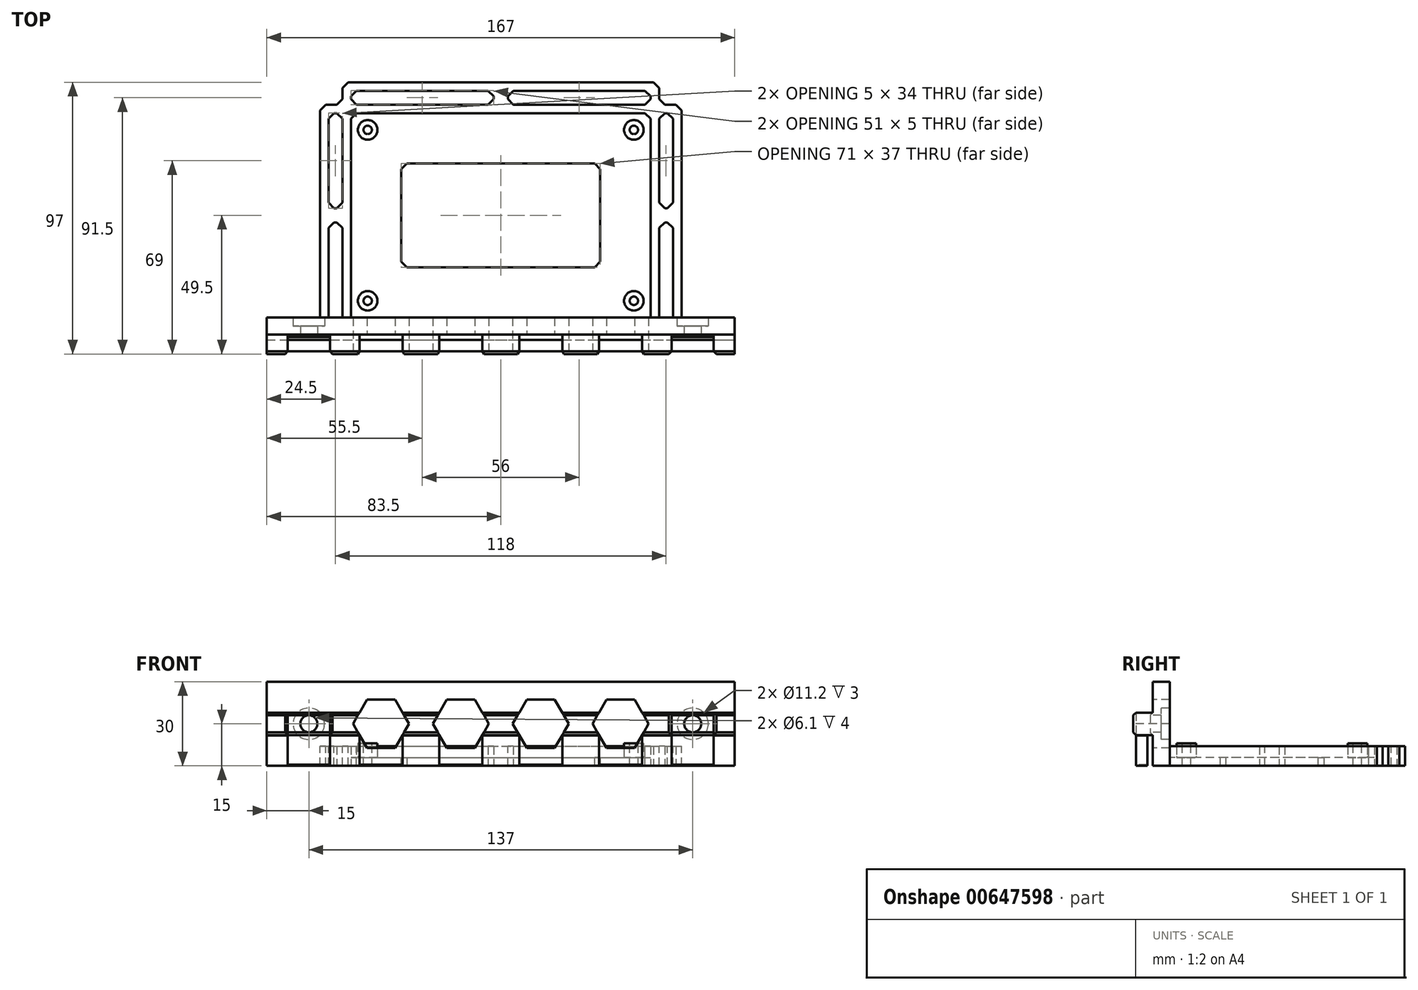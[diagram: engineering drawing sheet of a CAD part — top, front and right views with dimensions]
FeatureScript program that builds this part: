
annotation { "Feature Type Name" : "Feature", "Feature Type Description" : "" }
export const myFeature = defineFeature(function(context is Context, id is Id, definition is map)
    precondition{}
    {
        {
            var Q0;
            Q0=qCreatedBy(makeId("Top.planeOp"),FACE);
            var sketch = newSketch(context, id + "F0", { "sketchPlane" : qUnion([Q0])});
            skLineSegment(sketch, "E0.bottom", {"start": v(-47.5, 30.5) * mm, "end": v(47.5, 30.5) * mm, "construction": true});
            skLineSegment(sketch, "E0.top", {"start": v(-47.5, -30.5) * mm, "end": v(47.5, -30.5) * mm, "construction": true});
            skLineSegment(sketch, "E0.left", {"start": v(-47.5, 30.5) * mm, "end": v(-47.5, -30.5) * mm, "construction": true});
            skLineSegment(sketch, "E0.right", {"start": v(47.5, 30.5) * mm, "end": v(47.5, -30.5) * mm, "construction": true});
            skPoint(sketch, "E0.middle", {"position": v(0, 0) * mm});
            skCircle(sketch, "E1", {"center": v(-47.5, 30.5) * mm, "radius": 1.5 * mm});
            skCircle(sketch, "E2", {"center": v(47.5, 30.5) * mm, "radius": 1.5 * mm});
            skCircle(sketch, "E3", {"center": v(47.5, -30.5) * mm, "radius": 1.5 * mm});
            skCircle(sketch, "E4", {"center": v(-47.5, -30.5) * mm, "radius": 1.5 * mm});
            skCircle(sketch, "E5", {"center": v(-47.5, 30.5) * mm, "radius": 3.5 * mm});
            skCircle(sketch, "E6", {"center": v(47.5, 30.5) * mm, "radius": 3.5 * mm});
            skCircle(sketch, "E7", {"center": v(47.5, -30.5) * mm, "radius": 3.5 * mm});
            skCircle(sketch, "E8", {"center": v(-47.5, -30.5) * mm, "radius": 3.5 * mm});
            skLineSegment(sketch, "E9.0", {"start": v(-53.5, 44.5) * mm, "end": v(-53.5, -36.5) * mm});
            skLineSegment(sketch, "E9.1", {"start": v(-61.5, 36.5) * mm, "end": v(61.5, 36.5) * mm});
            skLineSegment(sketch, "E9.2", {"start": v(53.5, 44.5) * mm, "end": v(53.5, -36.5) * mm});
            skLineSegment(sketch, "E9.3", {"start": v(-83.5, -36.5) * mm, "end": v(83.5, -36.5) * mm});
            skLineSegment(sketch, "E10.0", {"start": v(-56.5, 47.5) * mm, "end": v(-56.5, -36.5) * mm});
            skLineSegment(sketch, "E10.1", {"start": v(-64.5, 39.5) * mm, "end": v(64.5, 39.5) * mm});
            skLineSegment(sketch, "E10.2", {"start": v(56.5, 47.5) * mm, "end": v(56.5, -36.5) * mm});
            skLineSegment(sketch, "E11.0", {"start": v(-61.5, 36.5) * mm, "end": v(-61.5, -36.5) * mm});
            skLineSegment(sketch, "E11.1", {"start": v(-53.5, 44.5) * mm, "end": v(53.5, 44.5) * mm});
            skLineSegment(sketch, "E11.2", {"start": v(61.5, 36.5) * mm, "end": v(61.5, -36.5) * mm});
            skLineSegment(sketch, "E12.0", {"start": v(-64.5, 39.5) * mm, "end": v(-64.5, -36.5) * mm});
            skLineSegment(sketch, "E12.1", {"start": v(-56.5, 47.5) * mm, "end": v(56.5, 47.5) * mm});
            skLineSegment(sketch, "E12.2", {"start": v(64.5, 39.5) * mm, "end": v(64.5, -36.5) * mm});
            skLineSegment(sketch, "E13.0", {"start": v(-35.5, 18.5) * mm, "end": v(-35.5, -18.5) * mm});
            skLineSegment(sketch, "E13.1", {"start": v(-35.5, 18.5) * mm, "end": v(35.5, 18.5) * mm});
            skLineSegment(sketch, "E13.2", {"start": v(35.5, 18.5) * mm, "end": v(35.5, -18.5) * mm});
            skLineSegment(sketch, "E13.3", {"start": v(-35.5, -18.5) * mm, "end": v(35.5, -18.5) * mm});
            skLineSegment(sketch, "E14", {"start": v(-83.5, -36.5) * mm, "end": v(-83.5, -42.5) * mm});
            skLineSegment(sketch, "E15", {"start": v(-83.5, -42.5) * mm, "end": v(83.5, -42.5) * mm});
            skLineSegment(sketch, "E16", {"start": v(83.5, -42.5) * mm, "end": v(83.5, -36.5) * mm});
            skPoint(sketch, "E17", {"position": v(0, -42.5) * mm});
            skLineSegment(sketch, "E18", {"start": v(-61.5, 2.5) * mm, "end": v(-56.5, 2.5) * mm});
            skLineSegment(sketch, "E19", {"start": v(-56.5, -2.5) * mm, "end": v(-61.5, -2.5) * mm});
            skLineSegment(sketch, "E20", {"start": v(-2.5, 44.5) * mm, "end": v(-2.5, 39.5) * mm});
            skLineSegment(sketch, "E21", {"start": v(2.5, 39.5) * mm, "end": v(2.5, 44.5) * mm});
            skLineSegment(sketch, "E22", {"start": v(56.5, 2.5) * mm, "end": v(61.5, 2.5) * mm});
            skLineSegment(sketch, "E23", {"start": v(61.5, -2.5) * mm, "end": v(56.5, -2.5) * mm});
            skPoint(sketch, "E24", {"position": v(0, 44.5) * mm});
            skPoint(sketch, "E25", {"position": v(-61.5, 0) * mm});
            skLineSegment(sketch, "E26", {"start": v(-61.5, 2.5) * mm, "end": v(-61.5, -2.5) * mm, "construction": true});
            skLineSegment(sketch, "E27", {"start": v(-2.5, 44.5) * mm, "end": v(2.5, 44.5) * mm, "construction": true});
            skSolve(sketch);
        }
        {
            var Q0;
            Q0=makeQuery(id+"F0.imprint","IMPRINT",FACE,{"disambiguationData":[TD([[makeQuery(id+"F0.imprint","IMPRINT",EDGE,{"derivedFrom":sQuery(id+"F0.wireOp",EDGE,"E5")}),-1.0]])]});
            var Q1;
            Q1=makeQuery(id+"F0.imprint","IMPRINT",FACE,{"disambiguationData":[TD([[makeQuery(id+"F0.imprint","IMPRINT",EDGE,{"derivedFrom":sQuery(id+"F0.wireOp",EDGE,"E1")}),-1.0]])]});
            var Q2;
            Q2=makeQuery(id+"F0.imprint","IMPRINT",FACE,{"disambiguationData":[TD([[makeQuery(id+"F0.imprint","IMPRINT",EDGE,{"derivedFrom":sQuery(id+"F0.wireOp",EDGE,"E4")}),-1.0]])]});
            var Q3;
            Q3=makeQuery(id+"F0.imprint","IMPRINT",FACE,{"disambiguationData":[TD([[makeQuery(id+"F0.imprint","IMPRINT",EDGE,{"derivedFrom":sQuery(id+"F0.wireOp",EDGE,"E3")}),-1.0]])]});
            var Q4;
            Q4=makeQuery(id+"F0.imprint","IMPRINT",FACE,{"disambiguationData":[TD([[makeQuery(id+"F0.imprint","IMPRINT",EDGE,{"derivedFrom":sQuery(id+"F0.wireOp",EDGE,"E2")}),-1.0]])]});
            var Q5;
            {var subQ0=sQuery(id+"F0.wireOp",EDGE,"E9.3");var subQ1=sQuery(id+"F0.wireOp",EDGE,"E9.0");var subQ2=makeQuery(id+"F0.imprint","INTERSECT",VERTEX,{"derivedFrom":[subQ1,subQ0]});Q5=makeQuery(id+"F0.imprint","IMPRINT",FACE,{"disambiguationData":[TD([[makeQuery(id+"F0.imprint","IMPRINT",EDGE,{"disambiguationData":[TD([[subQ2,1.0]])],"derivedFrom":subQ1}),-1.0]])]});}
            var Q6;
            {var subQ0=sQuery(id+"F0.wireOp",EDGE,"E12.0");Q6=makeQuery(id+"F0.imprint","IMPRINT",FACE,{"disambiguationData":[TD([[makeQuery(id+"F0.imprint","IMPRINT",EDGE,{"derivedFrom":subQ0}),1.0]])]});}
            var Q7;
            {var subQ0=sQuery(id+"F0.wireOp",EDGE,"E18");Q7=makeQuery(id+"F0.imprint","IMPRINT",FACE,{"disambiguationData":[TD([[makeQuery(id+"F0.imprint","IMPRINT",EDGE,{"derivedFrom":subQ0}),-1.0]])]});}
            var Q8;
            {var subQ0=sQuery(id+"F0.wireOp",EDGE,"E10.1");var subQ1=sQuery(id+"F0.wireOp",EDGE,"E9.0");var subQ2=makeQuery(id+"F0.imprint","INTERSECT",VERTEX,{"derivedFrom":[subQ1,subQ0]});Q8=makeQuery(id+"F0.imprint","IMPRINT",FACE,{"disambiguationData":[TD([[makeQuery(id+"F0.imprint","IMPRINT",EDGE,{"disambiguationData":[TD([[subQ2,-1.0]])],"derivedFrom":subQ1}),-1.0]])]});}
            var Q9;
            {var subQ13=sQuery(id+"F0.wireOp",EDGE,"E12.1");Q9=makeQuery(id+"F0.imprint","IMPRINT",FACE,{"disambiguationData":[TD([[makeQuery(id+"F0.imprint","IMPRINT",EDGE,{"derivedFrom":subQ13}),-1.0]])]});}
            var Q10;
            {var subQ0=sQuery(id+"F0.wireOp",EDGE,"E10.1");var subQ2=sQuery(id+"F0.wireOp",EDGE,"E9.0");var subQ3=makeQuery(id+"F0.imprint","INTERSECT",VERTEX,{"derivedFrom":[subQ2,subQ0]});Q10=makeQuery(id+"F0.imprint","IMPRINT",FACE,{"disambiguationData":[TD([[makeQuery(id+"F0.imprint","IMPRINT",EDGE,{"disambiguationData":[TD([[subQ3,-1.0]])],"derivedFrom":subQ2}),1.0]])]});}
            var Q11;
            {var subQ0=sQuery(id+"F0.wireOp",EDGE,"E14");Q11=makeQuery(id+"F0.imprint","IMPRINT",FACE,{"disambiguationData":[TD([[makeQuery(id+"F0.imprint","IMPRINT",EDGE,{"derivedFrom":subQ0}),1.0]])]});}
            var Q12;
            {var subQ0=sQuery(id+"F0.wireOp",EDGE,"E20");Q12=makeQuery(id+"F0.imprint","IMPRINT",FACE,{"disambiguationData":[TD([[makeQuery(id+"F0.imprint","IMPRINT",EDGE,{"derivedFrom":subQ0}),1.0]])]});}
            var Q13;
            {var subQ0=sQuery(id+"F0.wireOp",EDGE,"E9.2");var subQ1=sQuery(id+"F0.wireOp",EDGE,"E9.1");var subQ2=makeQuery(id+"F0.imprint","INTERSECT",VERTEX,{"derivedFrom":[subQ1,subQ0]});Q13=makeQuery(id+"F0.imprint","IMPRINT",FACE,{"disambiguationData":[TD([[makeQuery(id+"F0.imprint","IMPRINT",EDGE,{"disambiguationData":[TD([[subQ2,-1.0]])],"derivedFrom":subQ1}),1.0]])]});}
            var Q14;
            {var subQ0=sQuery(id+"F0.wireOp",EDGE,"E12.2");Q14=makeQuery(id+"F0.imprint","IMPRINT",FACE,{"disambiguationData":[TD([[makeQuery(id+"F0.imprint","IMPRINT",EDGE,{"derivedFrom":subQ0}),-1.0]])]});}
            var Q15;
            {var subQ0=sQuery(id+"F0.wireOp",EDGE,"E22");Q15=makeQuery(id+"F0.imprint","IMPRINT",FACE,{"disambiguationData":[TD([[makeQuery(id+"F0.imprint","IMPRINT",EDGE,{"derivedFrom":subQ0}),-1.0]])]});}
            var Q16;
            {var subQ2=sQuery(id+"F0.wireOp",EDGE,"E9.1");var subQ5=sQuery(id+"F0.wireOp",EDGE,"E9.2");var subQ7=makeQuery(id+"F0.imprint","INTERSECT",VERTEX,{"derivedFrom":[subQ2,subQ5]});Q16=makeQuery(id+"F0.imprint","IMPRINT",FACE,{"disambiguationData":[TD([[makeQuery(id+"F0.imprint","IMPRINT",EDGE,{"disambiguationData":[TD([[subQ7,-1.0]])],"derivedFrom":subQ2}),-1.0]])]});}
            extrude(context, id + "F1", {"entities" : qUnion([Q0, Q1, Q2, Q3, Q4, Q5, Q6, Q7, Q8, Q9, Q10, Q11, Q12, Q13, Q14, Q15, Q16]), "oppositeDirection" : true, "depth" : 3 * mm, "offsetDistance" : 25 * mm});
        }
        {
            var Q0;
            {var subQ0=sQuery(id+"F0.wireOp",EDGE,"E9.3");var subQ1=sQuery(id+"F0.wireOp",EDGE,"E9.0");var subQ2=makeQuery(id+"F0.imprint","INTERSECT",VERTEX,{"derivedFrom":[subQ1,subQ0]});Q0=makeQuery(id+"F0.imprint","IMPRINT",FACE,{"disambiguationData":[TD([[makeQuery(id+"F0.imprint","IMPRINT",EDGE,{"disambiguationData":[TD([[subQ2,1.0]])],"derivedFrom":subQ1}),-1.0]])]});}
            var Q1;
            {var subQ0=sQuery(id+"F0.wireOp",EDGE,"E10.1");var subQ1=sQuery(id+"F0.wireOp",EDGE,"E9.0");var subQ2=makeQuery(id+"F0.imprint","INTERSECT",VERTEX,{"derivedFrom":[subQ1,subQ0]});Q1=makeQuery(id+"F0.imprint","IMPRINT",FACE,{"disambiguationData":[TD([[makeQuery(id+"F0.imprint","IMPRINT",EDGE,{"disambiguationData":[TD([[subQ2,-1.0]])],"derivedFrom":subQ1}),-1.0]])]});}
            var Q2;
            {var subQ13=sQuery(id+"F0.wireOp",EDGE,"E12.1");Q2=makeQuery(id+"F0.imprint","IMPRINT",FACE,{"disambiguationData":[TD([[makeQuery(id+"F0.imprint","IMPRINT",EDGE,{"derivedFrom":subQ13}),-1.0]])]});}
            var Q3;
            {var subQ0=sQuery(id+"F0.wireOp",EDGE,"E12.0");Q3=makeQuery(id+"F0.imprint","IMPRINT",FACE,{"disambiguationData":[TD([[makeQuery(id+"F0.imprint","IMPRINT",EDGE,{"derivedFrom":subQ0}),1.0]])]});}
            var Q4;
            {var subQ0=sQuery(id+"F0.wireOp",EDGE,"E18");Q4=makeQuery(id+"F0.imprint","IMPRINT",FACE,{"disambiguationData":[TD([[makeQuery(id+"F0.imprint","IMPRINT",EDGE,{"derivedFrom":subQ0}),-1.0]])]});}
            var Q5;
            {var subQ0=sQuery(id+"F0.wireOp",EDGE,"E20");Q5=makeQuery(id+"F0.imprint","IMPRINT",FACE,{"disambiguationData":[TD([[makeQuery(id+"F0.imprint","IMPRINT",EDGE,{"derivedFrom":subQ0}),1.0]])]});}
            var Q6;
            {var subQ0=sQuery(id+"F0.wireOp",EDGE,"E10.1");var subQ2=sQuery(id+"F0.wireOp",EDGE,"E9.0");var subQ3=makeQuery(id+"F0.imprint","INTERSECT",VERTEX,{"derivedFrom":[subQ2,subQ0]});Q6=makeQuery(id+"F0.imprint","IMPRINT",FACE,{"disambiguationData":[TD([[makeQuery(id+"F0.imprint","IMPRINT",EDGE,{"disambiguationData":[TD([[subQ3,-1.0]])],"derivedFrom":subQ2}),1.0]])]});}
            var Q7;
            {var subQ0=sQuery(id+"F0.wireOp",EDGE,"E9.2");var subQ1=sQuery(id+"F0.wireOp",EDGE,"E9.1");var subQ2=makeQuery(id+"F0.imprint","INTERSECT",VERTEX,{"derivedFrom":[subQ1,subQ0]});Q7=makeQuery(id+"F0.imprint","IMPRINT",FACE,{"disambiguationData":[TD([[makeQuery(id+"F0.imprint","IMPRINT",EDGE,{"disambiguationData":[TD([[subQ2,-1.0]])],"derivedFrom":subQ1}),1.0]])]});}
            var Q8;
            {var subQ2=sQuery(id+"F0.wireOp",EDGE,"E9.1");var subQ5=sQuery(id+"F0.wireOp",EDGE,"E9.2");var subQ7=makeQuery(id+"F0.imprint","INTERSECT",VERTEX,{"derivedFrom":[subQ2,subQ5]});Q8=makeQuery(id+"F0.imprint","IMPRINT",FACE,{"disambiguationData":[TD([[makeQuery(id+"F0.imprint","IMPRINT",EDGE,{"disambiguationData":[TD([[subQ7,-1.0]])],"derivedFrom":subQ2}),-1.0]])]});}
            var Q9;
            {var subQ0=sQuery(id+"F0.wireOp",EDGE,"E12.2");Q9=makeQuery(id+"F0.imprint","IMPRINT",FACE,{"disambiguationData":[TD([[makeQuery(id+"F0.imprint","IMPRINT",EDGE,{"derivedFrom":subQ0}),-1.0]])]});}
            var Q10;
            {var subQ0=sQuery(id+"F0.wireOp",EDGE,"E22");Q10=makeQuery(id+"F0.imprint","IMPRINT",FACE,{"disambiguationData":[TD([[makeQuery(id+"F0.imprint","IMPRINT",EDGE,{"derivedFrom":subQ0}),-1.0]])]});}
            extrude(context, id + "F2", {"entities" : qUnion([Q0, Q1, Q2, Q3, Q4, Q5, Q6, Q7, Q8, Q9, Q10]), "operationType" : NewBodyOperationType.ADD, "depth" : 4 * mm, "offsetDistance" : 25 * mm});
        }
        {
            var Q0;
            Q0=makeQuery(id+"F0.imprint","IMPRINT",FACE,{"disambiguationData":[TD([[makeQuery(id+"F0.imprint","IMPRINT",EDGE,{"derivedFrom":sQuery(id+"F0.wireOp",EDGE,"E1")}),-1.0]])]});
            var Q1;
            Q1=makeQuery(id+"F0.imprint","IMPRINT",FACE,{"disambiguationData":[TD([[makeQuery(id+"F0.imprint","IMPRINT",EDGE,{"derivedFrom":sQuery(id+"F0.wireOp",EDGE,"E2")}),-1.0]])]});
            var Q2;
            Q2=makeQuery(id+"F0.imprint","IMPRINT",FACE,{"disambiguationData":[TD([[makeQuery(id+"F0.imprint","IMPRINT",EDGE,{"derivedFrom":sQuery(id+"F0.wireOp",EDGE,"E3")}),-1.0]])]});
            var Q3;
            Q3=makeQuery(id+"F0.imprint","IMPRINT",FACE,{"disambiguationData":[TD([[makeQuery(id+"F0.imprint","IMPRINT",EDGE,{"derivedFrom":sQuery(id+"F0.wireOp",EDGE,"E4")}),-1.0]])]});
            extrude(context, id + "F3", {"entities" : qUnion([Q0, Q1, Q2, Q3]), "operationType" : NewBodyOperationType.ADD, "depth" : 5 * mm, "offsetDistance" : 25 * mm});
        }
        {
            var Q0;
            {var subQ0=sQuery(id+"F0.wireOp",EDGE,"E14");Q0=makeQuery(id+"F0.imprint","IMPRINT",FACE,{"disambiguationData":[TD([[makeQuery(id+"F0.imprint","IMPRINT",EDGE,{"derivedFrom":subQ0}),1.0]])]});}
            extrude(context, id + "F4", {"entities" : qUnion([Q0]), "operationType" : NewBodyOperationType.ADD, "depth" : 27 * mm, "offsetDistance" : 25 * mm});
        }
        {
            var Q0;
            {var subQ0=sQuery(id+"F0.wireOp",EDGE,"E15");Q0=makeQuery(id+"F4.boolean.opBoolean","MERGE",FACE,{"derivedFrom":[makeQuery(id+"F1.opExtrude","SWEPT_FACE",FACE,{"disambiguationData":[OSD([subQ0])]}),makeQuery(id+"F4.opExtrude","SWEPT_FACE",FACE,{"disambiguationData":[OSD([subQ0])]})]});}
            var sketch = newSketch(context, id + "F5", { "sketchPlane" : qUnion([Q0])});
            skLineSegment(sketch, "E28.bottom", {"start": v(-83.5, 16) * mm, "end": v(83.5, 16) * mm});
            skLineSegment(sketch, "E28.top", {"start": v(-83.5, 8) * mm, "end": v(83.5, 8) * mm});
            skLineSegment(sketch, "E28.left", {"start": v(-83.5, 16) * mm, "end": v(-83.5, 8) * mm});
            skLineSegment(sketch, "E28.right", {"start": v(83.5, 16) * mm, "end": v(83.5, 8) * mm});
            skPoint(sketch, "E29", {"position": v(-83.5, 12) * mm});
            skCircle(sketch, "E30", {"center": v(-68.5, 12) * mm, "radius": 3.05 * mm});
            skCircle(sketch, "E31", {"center": v(-68.5, 12) * mm, "radius": 5.6 * mm});
            skCircle(sketch, "E32", {"center": v(68.5, 12) * mm, "radius": 3.05 * mm});
            skCircle(sketch, "E33", {"center": v(68.5, 12) * mm, "radius": 5.6 * mm});
            skCircle(sketch, "E34.cCircle", {"center": v(-42.75, 12) * mm, "radius": 10 * mm, "construction": true});
            skLineSegment(sketch, "E34.0", {"start": v(-32.75, 12) * mm, "end": v(-37.75, 3.34) * mm});
            skLineSegment(sketch, "E34.1", {"start": v(-37.75, 3.34) * mm, "end": v(-47.75, 3.34) * mm});
            skLineSegment(sketch, "E34.2", {"start": v(-47.75, 3.34) * mm, "end": v(-52.75, 12) * mm});
            skLineSegment(sketch, "E34.3", {"start": v(-52.75, 12) * mm, "end": v(-47.75, 20.66) * mm});
            skLineSegment(sketch, "E34.4", {"start": v(-47.75, 20.66) * mm, "end": v(-37.75, 20.66) * mm});
            skLineSegment(sketch, "E34.5", {"start": v(-37.75, 20.66) * mm, "end": v(-32.75, 12) * mm});
            skCircle(sketch, "E35.cCircle", {"center": v(-14.25, 12) * mm, "radius": 10 * mm, "construction": true});
            skLineSegment(sketch, "E35.0", {"start": v(-4.25, 12) * mm, "end": v(-9.25, 3.34) * mm});
            skLineSegment(sketch, "E35.1", {"start": v(-9.25, 3.34) * mm, "end": v(-19.25, 3.34) * mm});
            skLineSegment(sketch, "E35.2", {"start": v(-19.25, 3.34) * mm, "end": v(-24.25, 12) * mm});
            skLineSegment(sketch, "E35.3", {"start": v(-24.25, 12) * mm, "end": v(-19.25, 20.66) * mm});
            skLineSegment(sketch, "E35.4", {"start": v(-19.25, 20.66) * mm, "end": v(-9.25, 20.66) * mm});
            skLineSegment(sketch, "E35.5", {"start": v(-9.25, 20.66) * mm, "end": v(-4.25, 12) * mm});
            skCircle(sketch, "E36.cCircle", {"center": v(14.25, 12) * mm, "radius": 10 * mm, "construction": true});
            skLineSegment(sketch, "E36.0", {"start": v(24.25, 12) * mm, "end": v(19.25, 3.34) * mm});
            skLineSegment(sketch, "E36.1", {"start": v(19.25, 3.34) * mm, "end": v(9.25, 3.34) * mm});
            skLineSegment(sketch, "E36.2", {"start": v(9.25, 3.34) * mm, "end": v(4.25, 12) * mm});
            skLineSegment(sketch, "E36.3", {"start": v(4.25, 12) * mm, "end": v(9.25, 20.66) * mm});
            skLineSegment(sketch, "E36.4", {"start": v(9.25, 20.66) * mm, "end": v(19.25, 20.66) * mm});
            skLineSegment(sketch, "E36.5", {"start": v(19.25, 20.66) * mm, "end": v(24.25, 12) * mm});
            skCircle(sketch, "E37.cCircle", {"center": v(42.75, 12) * mm, "radius": 10 * mm, "construction": true});
            skLineSegment(sketch, "E37.0", {"start": v(52.75, 12) * mm, "end": v(47.75, 3.34) * mm});
            skLineSegment(sketch, "E37.1", {"start": v(47.75, 3.34) * mm, "end": v(37.75, 3.34) * mm});
            skLineSegment(sketch, "E37.2", {"start": v(37.75, 3.34) * mm, "end": v(32.75, 12) * mm});
            skLineSegment(sketch, "E37.3", {"start": v(32.75, 12) * mm, "end": v(37.75, 20.66) * mm});
            skLineSegment(sketch, "E37.4", {"start": v(37.75, 20.66) * mm, "end": v(47.75, 20.66) * mm});
            skLineSegment(sketch, "E37.5", {"start": v(47.75, 20.66) * mm, "end": v(52.75, 12) * mm});
            skLineSegment(sketch, "E38", {"start": v(-32.75, 12) * mm, "end": v(-24.25, 12) * mm, "construction": true});
            skLineSegment(sketch, "E39", {"start": v(-4.25, 12) * mm, "end": v(4.25, 12) * mm, "construction": true});
            skLineSegment(sketch, "E40", {"start": v(24.25, 12) * mm, "end": v(32.75, 12) * mm, "construction": true});
            skLineSegment(sketch, "E41", {"start": v(-68.5, 12) * mm, "end": v(-52.75, 12) * mm, "construction": true});
            skLineSegment(sketch, "E42", {"start": v(52.75, 12) * mm, "end": v(68.5, 12) * mm, "construction": true});
            skLineSegment(sketch, "E43", {"start": v(-83.5, 12) * mm, "end": v(-68.5, 12) * mm, "construction": true});
            skLineSegment(sketch, "E44", {"start": v(68.5, 12) * mm, "end": v(83.5, 12) * mm, "construction": true});
            skLineSegment(sketch, "E45", {"start": v(-76, 16) * mm, "end": v(-76, 8) * mm});
            skLineSegment(sketch, "E46", {"start": v(-61, 8) * mm, "end": v(-61, 16) * mm});
            skLineSegment(sketch, "E47", {"start": v(76, 16) * mm, "end": v(76, 8) * mm});
            skLineSegment(sketch, "E48", {"start": v(61, 8) * mm, "end": v(61, 16) * mm});
            skLineSegment(sketch, "E49", {"start": v(-76, 12) * mm, "end": v(-61, 12) * mm, "construction": true});
            skLineSegment(sketch, "E50", {"start": v(61, 12) * mm, "end": v(76, 12) * mm, "construction": true});
            skPoint(sketch, "E50.endSnap0", {"position": v(76, 12) * mm});
            skSolve(sketch);
        }
        {
            var Q0;
            {var subQ0=sQuery(id+"F5.wireOp",EDGE,"E31");var subQ1=sQuery(id+"F5.wireOp",EDGE,"E28.bottom");var subQ2=makeQuery(id+"F5.imprint","INTERSECT",VERTEX,{"disambiguationData":[OD(0.0)],"derivedFrom":[subQ1,subQ0]});Q0=makeQuery(id+"F5.imprint","IMPRINT",FACE,{"disambiguationData":[TD([[makeQuery(id+"F5.imprint","IMPRINT",EDGE,{"disambiguationData":[TD([[subQ2,-1.0]])],"derivedFrom":subQ1}),1.0]])]});}
            var Q1;
            {var subQ0=sQuery(id+"F5.wireOp",EDGE,"E31");var subQ1=sQuery(id+"F5.wireOp",EDGE,"E28.top");var subQ2=makeQuery(id+"F5.imprint","INTERSECT",VERTEX,{"disambiguationData":[OD(0.0)],"derivedFrom":[subQ1,subQ0]});Q1=makeQuery(id+"F5.imprint","IMPRINT",FACE,{"disambiguationData":[TD([[makeQuery(id+"F5.imprint","IMPRINT",EDGE,{"disambiguationData":[TD([[subQ2,-1.0]])],"derivedFrom":subQ1}),-1.0]])]});}
            var Q2;
            Q2=makeQuery(id+"F5.imprint","IMPRINT",FACE,{"disambiguationData":[TD([[makeQuery(id+"F5.imprint","IMPRINT",EDGE,{"derivedFrom":sQuery(id+"F5.wireOp",EDGE,"E30")}),-1.0]])]});
            var Q3;
            Q3=makeQuery(id+"F5.imprint","IMPRINT",FACE,{"disambiguationData":[TD([[makeQuery(id+"F5.imprint","IMPRINT",EDGE,{"derivedFrom":sQuery(id+"F5.wireOp",EDGE,"E30")}),1.0]])]});
            var Q4;
            {var subQ5=sQuery(id+"F5.wireOp",EDGE,"E34.4");Q4=makeQuery(id+"F5.imprint","IMPRINT",FACE,{"disambiguationData":[TD([[makeQuery(id+"F5.imprint","IMPRINT",EDGE,{"derivedFrom":subQ5}),-1.0]])]});}
            var Q5;
            {var subQ7=sQuery(id+"F5.wireOp",EDGE,"E28.bottom");var subQ9=sQuery(id+"F5.wireOp",EDGE,"E34.3");var subQ11=makeQuery(id+"F5.imprint","INTERSECT",VERTEX,{"derivedFrom":[subQ7,subQ9]});Q5=makeQuery(id+"F5.imprint","IMPRINT",FACE,{"disambiguationData":[TD([[makeQuery(id+"F5.imprint","IMPRINT",EDGE,{"disambiguationData":[TD([[subQ11,-1.0]])],"derivedFrom":subQ7}),-1.0]])]});}
            var Q6;
            {var subQ5=sQuery(id+"F5.wireOp",EDGE,"E34.1");Q6=makeQuery(id+"F5.imprint","IMPRINT",FACE,{"disambiguationData":[TD([[makeQuery(id+"F5.imprint","IMPRINT",EDGE,{"derivedFrom":subQ5}),-1.0]])]});}
            var Q7;
            {var subQ5=sQuery(id+"F5.wireOp",EDGE,"E35.1");Q7=makeQuery(id+"F5.imprint","IMPRINT",FACE,{"disambiguationData":[TD([[makeQuery(id+"F5.imprint","IMPRINT",EDGE,{"derivedFrom":subQ5}),-1.0]])]});}
            var Q8;
            {var subQ0=sQuery(id+"F5.wireOp",EDGE,"E35.3");var subQ9=sQuery(id+"F5.wireOp",EDGE,"E28.bottom");var subQ10=makeQuery(id+"F5.imprint","INTERSECT",VERTEX,{"derivedFrom":[subQ9,subQ0]});Q8=makeQuery(id+"F5.imprint","IMPRINT",FACE,{"disambiguationData":[TD([[makeQuery(id+"F5.imprint","IMPRINT",EDGE,{"disambiguationData":[TD([[subQ10,-1.0]])],"derivedFrom":subQ9}),-1.0]])]});}
            var Q9;
            {var subQ5=sQuery(id+"F5.wireOp",EDGE,"E35.4");Q9=makeQuery(id+"F5.imprint","IMPRINT",FACE,{"disambiguationData":[TD([[makeQuery(id+"F5.imprint","IMPRINT",EDGE,{"derivedFrom":subQ5}),-1.0]])]});}
            var Q10;
            {var subQ5=sQuery(id+"F5.wireOp",EDGE,"E36.4");Q10=makeQuery(id+"F5.imprint","IMPRINT",FACE,{"disambiguationData":[TD([[makeQuery(id+"F5.imprint","IMPRINT",EDGE,{"derivedFrom":subQ5}),-1.0]])]});}
            var Q11;
            {var subQ0=sQuery(id+"F5.wireOp",EDGE,"E36.3");var subQ9=sQuery(id+"F5.wireOp",EDGE,"E28.bottom");var subQ10=makeQuery(id+"F5.imprint","INTERSECT",VERTEX,{"derivedFrom":[subQ9,subQ0]});Q11=makeQuery(id+"F5.imprint","IMPRINT",FACE,{"disambiguationData":[TD([[makeQuery(id+"F5.imprint","IMPRINT",EDGE,{"disambiguationData":[TD([[subQ10,-1.0]])],"derivedFrom":subQ9}),-1.0]])]});}
            var Q12;
            {var subQ5=sQuery(id+"F5.wireOp",EDGE,"E36.1");Q12=makeQuery(id+"F5.imprint","IMPRINT",FACE,{"disambiguationData":[TD([[makeQuery(id+"F5.imprint","IMPRINT",EDGE,{"derivedFrom":subQ5}),-1.0]])]});}
            var Q13;
            {var subQ5=sQuery(id+"F5.wireOp",EDGE,"E37.1");Q13=makeQuery(id+"F5.imprint","IMPRINT",FACE,{"disambiguationData":[TD([[makeQuery(id+"F5.imprint","IMPRINT",EDGE,{"derivedFrom":subQ5}),-1.0]])]});}
            var Q14;
            {var subQ0=sQuery(id+"F5.wireOp",EDGE,"E37.3");var subQ9=sQuery(id+"F5.wireOp",EDGE,"E28.bottom");var subQ10=makeQuery(id+"F5.imprint","INTERSECT",VERTEX,{"derivedFrom":[subQ9,subQ0]});Q14=makeQuery(id+"F5.imprint","IMPRINT",FACE,{"disambiguationData":[TD([[makeQuery(id+"F5.imprint","IMPRINT",EDGE,{"disambiguationData":[TD([[subQ10,-1.0]])],"derivedFrom":subQ9}),-1.0]])]});}
            var Q15;
            {var subQ5=sQuery(id+"F5.wireOp",EDGE,"E37.4");Q15=makeQuery(id+"F5.imprint","IMPRINT",FACE,{"disambiguationData":[TD([[makeQuery(id+"F5.imprint","IMPRINT",EDGE,{"derivedFrom":subQ5}),-1.0]])]});}
            var Q16;
            {var subQ0=sQuery(id+"F5.wireOp",EDGE,"E33");var subQ1=sQuery(id+"F5.wireOp",EDGE,"E28.bottom");var subQ2=makeQuery(id+"F5.imprint","INTERSECT",VERTEX,{"disambiguationData":[OD(0.0)],"derivedFrom":[subQ1,subQ0]});Q16=makeQuery(id+"F5.imprint","IMPRINT",FACE,{"disambiguationData":[TD([[makeQuery(id+"F5.imprint","IMPRINT",EDGE,{"disambiguationData":[TD([[subQ2,-1.0]])],"derivedFrom":subQ1}),1.0]])]});}
            var Q17;
            Q17=makeQuery(id+"F5.imprint","IMPRINT",FACE,{"disambiguationData":[TD([[makeQuery(id+"F5.imprint","IMPRINT",EDGE,{"derivedFrom":sQuery(id+"F5.wireOp",EDGE,"E32")}),-1.0]])]});
            var Q18;
            {var subQ0=sQuery(id+"F5.wireOp",EDGE,"E33");var subQ1=sQuery(id+"F5.wireOp",EDGE,"E28.top");var subQ2=makeQuery(id+"F5.imprint","INTERSECT",VERTEX,{"disambiguationData":[OD(0.0)],"derivedFrom":[subQ1,subQ0]});Q18=makeQuery(id+"F5.imprint","IMPRINT",FACE,{"disambiguationData":[TD([[makeQuery(id+"F5.imprint","IMPRINT",EDGE,{"disambiguationData":[TD([[subQ2,-1.0]])],"derivedFrom":subQ1}),-1.0]])]});}
            var Q19;
            Q19=makeQuery(id+"F5.imprint","IMPRINT",FACE,{"disambiguationData":[TD([[makeQuery(id+"F5.imprint","IMPRINT",EDGE,{"derivedFrom":sQuery(id+"F5.wireOp",EDGE,"E32")}),1.0]])]});
            var Q20;
            {var subQ0=sQuery(id+"F0.wireOp",EDGE,"E9.3");Q20=makeQuery(id+"F4.boolean.opBoolean","MERGE",FACE,{"derivedFrom":[makeQuery(id+"F1.opExtrude","SWEPT_FACE",FACE,{"disambiguationData":[OSD([subQ0]),TDD([makeQuery(id+"F0.imprint","IMPRINT",EDGE,{"disambiguationData":[TD([[makeQuery(id+"F0.imprint","INTERSECT",VERTEX,{"derivedFrom":[subQ0,sQuery(id+"F0.wireOp",EDGE,"E14")]}),-1.0]])],"derivedFrom":subQ0})])]}),makeQuery(id+"F1.opExtrude","SWEPT_FACE",FACE,{"disambiguationData":[OSD([subQ0]),TDD([makeQuery(id+"F0.imprint","IMPRINT",EDGE,{"disambiguationData":[TD([[makeQuery(id+"F0.imprint","INTERSECT",VERTEX,{"derivedFrom":[subQ0,sQuery(id+"F0.wireOp",EDGE,"E10.0")]}),1.0]])],"derivedFrom":subQ0})])]}),makeQuery(id+"F1.opExtrude","SWEPT_FACE",FACE,{"disambiguationData":[OSD([subQ0]),TDD([makeQuery(id+"F0.imprint","IMPRINT",EDGE,{"disambiguationData":[TD([[makeQuery(id+"F0.imprint","INTERSECT",VERTEX,{"derivedFrom":[subQ0,sQuery(id+"F0.wireOp",EDGE,"E10.2")]}),-1.0]])],"derivedFrom":subQ0})])]}),makeQuery(id+"F1.opExtrude","SWEPT_FACE",FACE,{"disambiguationData":[OSD([subQ0]),TDD([makeQuery(id+"F0.imprint","IMPRINT",EDGE,{"disambiguationData":[TD([[makeQuery(id+"F0.imprint","INTERSECT",VERTEX,{"derivedFrom":[subQ0,sQuery(id+"F0.wireOp",EDGE,"E16")]}),1.0]])],"derivedFrom":subQ0})])]}),makeQuery(id+"F4.opExtrude","SWEPT_FACE",FACE,{"disambiguationData":[OSD([subQ0])]})]});}
            extrude(context, id + "F6", {"entities" : qUnion([Q0, Q1, Q2, Q3, Q4, Q5, Q6, Q7, Q8, Q9, Q10, Q11, Q12, Q13, Q14, Q15, Q16, Q17, Q18, Q19]), "operationType" : NewBodyOperationType.REMOVE, "endBound" : BoundingType.UP_TO_SURFACE, "oppositeDirection" : true, "depth" : 25 * mm, "endBoundEntityFace" : qUnion([Q20]), "offsetDistance" : 25 * mm});
        }
        {
            var Q0;
            {var subQ0=sQuery(id+"F5.wireOp",EDGE,"E31");var subQ1=sQuery(id+"F5.wireOp",EDGE,"E28.bottom");var subQ2=makeQuery(id+"F5.imprint","INTERSECT",VERTEX,{"disambiguationData":[OD(0.0)],"derivedFrom":[subQ1,subQ0]});Q0=makeQuery(id+"F5.imprint","IMPRINT",FACE,{"disambiguationData":[TD([[makeQuery(id+"F5.imprint","IMPRINT",EDGE,{"disambiguationData":[TD([[subQ2,-1.0]])],"derivedFrom":subQ1}),1.0]])]});}
            var Q1;
            Q1=makeQuery(id+"F5.imprint","IMPRINT",FACE,{"disambiguationData":[TD([[makeQuery(id+"F5.imprint","IMPRINT",EDGE,{"derivedFrom":sQuery(id+"F5.wireOp",EDGE,"E30")}),-1.0]])]});
            var Q2;
            {var subQ0=sQuery(id+"F5.wireOp",EDGE,"E31");var subQ1=sQuery(id+"F5.wireOp",EDGE,"E28.top");var subQ2=makeQuery(id+"F5.imprint","INTERSECT",VERTEX,{"disambiguationData":[OD(0.0)],"derivedFrom":[subQ1,subQ0]});Q2=makeQuery(id+"F5.imprint","IMPRINT",FACE,{"disambiguationData":[TD([[makeQuery(id+"F5.imprint","IMPRINT",EDGE,{"disambiguationData":[TD([[subQ2,-1.0]])],"derivedFrom":subQ1}),-1.0]])]});}
            var Q3;
            {var subQ0=sQuery(id+"F5.wireOp",EDGE,"E33");var subQ1=sQuery(id+"F5.wireOp",EDGE,"E28.top");var subQ2=makeQuery(id+"F5.imprint","INTERSECT",VERTEX,{"disambiguationData":[OD(0.0)],"derivedFrom":[subQ1,subQ0]});Q3=makeQuery(id+"F5.imprint","IMPRINT",FACE,{"disambiguationData":[TD([[makeQuery(id+"F5.imprint","IMPRINT",EDGE,{"disambiguationData":[TD([[subQ2,-1.0]])],"derivedFrom":subQ1}),-1.0]])]});}
            var Q4;
            Q4=makeQuery(id+"F5.imprint","IMPRINT",FACE,{"disambiguationData":[TD([[makeQuery(id+"F5.imprint","IMPRINT",EDGE,{"derivedFrom":sQuery(id+"F5.wireOp",EDGE,"E32")}),-1.0]])]});
            var Q5;
            {var subQ0=sQuery(id+"F5.wireOp",EDGE,"E33");var subQ1=sQuery(id+"F5.wireOp",EDGE,"E28.bottom");var subQ2=makeQuery(id+"F5.imprint","INTERSECT",VERTEX,{"disambiguationData":[OD(0.0)],"derivedFrom":[subQ1,subQ0]});Q5=makeQuery(id+"F5.imprint","IMPRINT",FACE,{"disambiguationData":[TD([[makeQuery(id+"F5.imprint","IMPRINT",EDGE,{"disambiguationData":[TD([[subQ2,-1.0]])],"derivedFrom":subQ1}),1.0]])]});}
            var Q6;
            {var subQ0=sQuery(id+"F0.wireOp",EDGE,"E9.3");Q6=makeQuery(id+"F4.boolean.opBoolean","MERGE",FACE,{"derivedFrom":[makeQuery(id+"F1.opExtrude","SWEPT_FACE",FACE,{"disambiguationData":[OSD([subQ0]),TDD([makeQuery(id+"F0.imprint","IMPRINT",EDGE,{"disambiguationData":[TD([[makeQuery(id+"F0.imprint","INTERSECT",VERTEX,{"derivedFrom":[subQ0,sQuery(id+"F0.wireOp",EDGE,"E14")]}),-1.0]])],"derivedFrom":subQ0})])]}),makeQuery(id+"F1.opExtrude","SWEPT_FACE",FACE,{"disambiguationData":[OSD([subQ0]),TDD([makeQuery(id+"F0.imprint","IMPRINT",EDGE,{"disambiguationData":[TD([[makeQuery(id+"F0.imprint","INTERSECT",VERTEX,{"derivedFrom":[subQ0,sQuery(id+"F0.wireOp",EDGE,"E10.0")]}),1.0]])],"derivedFrom":subQ0})])]}),makeQuery(id+"F1.opExtrude","SWEPT_FACE",FACE,{"disambiguationData":[OSD([subQ0]),TDD([makeQuery(id+"F0.imprint","IMPRINT",EDGE,{"disambiguationData":[TD([[makeQuery(id+"F0.imprint","INTERSECT",VERTEX,{"derivedFrom":[subQ0,sQuery(id+"F0.wireOp",EDGE,"E10.2")]}),-1.0]])],"derivedFrom":subQ0})])]}),makeQuery(id+"F1.opExtrude","SWEPT_FACE",FACE,{"disambiguationData":[OSD([subQ0]),TDD([makeQuery(id+"F0.imprint","IMPRINT",EDGE,{"disambiguationData":[TD([[makeQuery(id+"F0.imprint","INTERSECT",VERTEX,{"derivedFrom":[subQ0,sQuery(id+"F0.wireOp",EDGE,"E16")]}),1.0]])],"derivedFrom":subQ0})])]}),makeQuery(id+"F4.opExtrude","SWEPT_FACE",FACE,{"disambiguationData":[OSD([subQ0])]})]});}
            extrude(context, id + "F7", {"entities" : qUnion([Q0, Q1, Q2, Q3, Q4, Q5]), "operationType" : NewBodyOperationType.ADD, "endBound" : BoundingType.UP_TO_SURFACE, "oppositeDirection" : true, "depth" : 25 * mm, "endBoundEntityFace" : qUnion([Q6]), "hasOffset" : true, "offsetDistance" : 3 * mm});
        }
        {
            var Q0;
            {var subQ0=sQuery(id+"F5.wireOp",EDGE,"E28.left");Q0=makeQuery(id+"F5.imprint","IMPRINT",FACE,{"disambiguationData":[TD([[makeQuery(id+"F5.imprint","IMPRINT",EDGE,{"derivedFrom":subQ0}),-1.0]])]});}
            var Q1;
            {var subQ0=sQuery(id+"F5.wireOp",EDGE,"E28.right");Q1=makeQuery(id+"F5.imprint","IMPRINT",FACE,{"disambiguationData":[TD([[makeQuery(id+"F5.imprint","IMPRINT",EDGE,{"derivedFrom":subQ0}),1.0]])]});}
            var Q2;
            {var subQ7=sQuery(id+"F5.wireOp",EDGE,"E48");Q2=makeQuery(id+"F5.imprint","IMPRINT",FACE,{"disambiguationData":[TD([[makeQuery(id+"F5.imprint","IMPRINT",EDGE,{"derivedFrom":subQ7}),1.0]])]});}
            var Q3;
            {var subQ0=sQuery(id+"F5.wireOp",EDGE,"E36.5");var subQ7=sQuery(id+"F5.wireOp",EDGE,"E28.bottom");var subQ8=makeQuery(id+"F5.imprint","INTERSECT",VERTEX,{"derivedFrom":[subQ7,subQ0]});Q3=makeQuery(id+"F5.imprint","IMPRINT",FACE,{"disambiguationData":[TD([[makeQuery(id+"F5.imprint","IMPRINT",EDGE,{"disambiguationData":[TD([[subQ8,-1.0]])],"derivedFrom":subQ7}),-1.0]])]});}
            var Q4;
            {var subQ0=sQuery(id+"F5.wireOp",EDGE,"E35.5");var subQ5=sQuery(id+"F5.wireOp",EDGE,"E28.bottom");var subQ6=makeQuery(id+"F5.imprint","INTERSECT",VERTEX,{"derivedFrom":[subQ5,subQ0]});Q4=makeQuery(id+"F5.imprint","IMPRINT",FACE,{"disambiguationData":[TD([[makeQuery(id+"F5.imprint","IMPRINT",EDGE,{"disambiguationData":[TD([[subQ6,-1.0]])],"derivedFrom":subQ5}),-1.0]])]});}
            var Q5;
            {var subQ0=sQuery(id+"F5.wireOp",EDGE,"E34.5");var subQ3=sQuery(id+"F5.wireOp",EDGE,"E28.bottom");var subQ4=makeQuery(id+"F5.imprint","INTERSECT",VERTEX,{"derivedFrom":[subQ3,subQ0]});Q5=makeQuery(id+"F5.imprint","IMPRINT",FACE,{"disambiguationData":[TD([[makeQuery(id+"F5.imprint","IMPRINT",EDGE,{"disambiguationData":[TD([[subQ4,-1.0]])],"derivedFrom":subQ3}),-1.0]])]});}
            var Q6;
            {var subQ7=sQuery(id+"F5.wireOp",EDGE,"E46");Q6=makeQuery(id+"F5.imprint","IMPRINT",FACE,{"disambiguationData":[TD([[makeQuery(id+"F5.imprint","IMPRINT",EDGE,{"derivedFrom":subQ7}),-1.0]])]});}
            extrude(context, id + "F8", {"entities" : qUnion([Q0, Q1, Q2, Q3, Q4, Q5, Q6]), "operationType" : NewBodyOperationType.ADD, "depth" : 7 * mm, "offsetDistance" : 25 * mm});
        }
        {
            var Q0;
            Q0=makeQuery(id+"F5.imprint","IMPRINT",FACE,{"disambiguationData":[TD([[makeQuery(id+"F5.imprint","IMPRINT",EDGE,{"derivedFrom":sQuery(id+"F5.wireOp",EDGE,"E30")}),-1.0]])]});
            var Q1;
            {var subQ0=sQuery(id+"F5.wireOp",EDGE,"E46");Q1=makeQuery(id+"F5.imprint","IMPRINT",FACE,{"disambiguationData":[TD([[makeQuery(id+"F5.imprint","IMPRINT",EDGE,{"derivedFrom":subQ0}),1.0]])]});}
            var Q2;
            {var subQ0=sQuery(id+"F5.wireOp",EDGE,"E45");Q2=makeQuery(id+"F5.imprint","IMPRINT",FACE,{"disambiguationData":[TD([[makeQuery(id+"F5.imprint","IMPRINT",EDGE,{"derivedFrom":subQ0}),1.0]])]});}
            var Q3;
            {var subQ0=sQuery(id+"F5.wireOp",EDGE,"E48");Q3=makeQuery(id+"F5.imprint","IMPRINT",FACE,{"disambiguationData":[TD([[makeQuery(id+"F5.imprint","IMPRINT",EDGE,{"derivedFrom":subQ0}),-1.0]])]});}
            var Q4;
            Q4=makeQuery(id+"F5.imprint","IMPRINT",FACE,{"disambiguationData":[TD([[makeQuery(id+"F5.imprint","IMPRINT",EDGE,{"derivedFrom":sQuery(id+"F5.wireOp",EDGE,"E32")}),-1.0]])]});
            var Q5;
            {var subQ0=sQuery(id+"F5.wireOp",EDGE,"E47");Q5=makeQuery(id+"F5.imprint","IMPRINT",FACE,{"disambiguationData":[TD([[makeQuery(id+"F5.imprint","IMPRINT",EDGE,{"derivedFrom":subQ0}),-1.0]])]});}
            extrude(context, id + "F9", {"entities" : qUnion([Q0, Q1, Q2, Q3, Q4, Q5]), "operationType" : NewBodyOperationType.ADD, "depth" : 1 * mm, "offsetDistance" : 25 * mm});
        }
        {
            var Q0;
            {var subQ0=sQuery(id+"F5.wireOp",EDGE,"E28.top");Q0=makeQuery(id+"F8.opExtrude","CAP_EDGE",EDGE,{"disambiguationData":[OSD([subQ0]),TDD([makeQuery(id+"F5.imprint","IMPRINT",EDGE,{"disambiguationData":[TD([[makeQuery(id+"F5.imprint","INTERSECT",VERTEX,{"derivedFrom":[subQ0,sQuery(id+"F5.wireOp",EDGE,"E45")]}),1.0]])],"derivedFrom":subQ0})])],"isStart":false});}
            var Q1;
            {var subQ0=sQuery(id+"F5.wireOp",EDGE,"E28.bottom");Q1=makeQuery(id+"F8.opExtrude","CAP_EDGE",EDGE,{"disambiguationData":[OSD([subQ0]),TDD([makeQuery(id+"F5.imprint","IMPRINT",EDGE,{"disambiguationData":[TD([[makeQuery(id+"F5.imprint","INTERSECT",VERTEX,{"derivedFrom":[subQ0,sQuery(id+"F5.wireOp",EDGE,"E45")]}),1.0]])],"derivedFrom":subQ0})])],"isStart":false});}
            var Q2;
            {var subQ0=sQuery(id+"F5.wireOp",EDGE,"E28.bottom");var subQ1=sQuery(id+"F5.wireOp",EDGE,"E31");var subQ3=makeQuery(id+"F5.imprint","INTERSECT",VERTEX,{"disambiguationData":[OD(0.0)],"derivedFrom":[subQ0,subQ1]});Q2=makeQuery(id+"F9.opExtrude","CAP_EDGE",EDGE,{"disambiguationData":[OSD([subQ0]),TDD([makeQuery(id+"F5.imprint","IMPRINT",EDGE,{"disambiguationData":[TD([[makeQuery(id+"F5.imprint","INTERSECT",VERTEX,{"derivedFrom":[subQ0,sQuery(id+"F5.wireOp",EDGE,"E45")]}),-1.0]])],"derivedFrom":subQ0}),makeQuery(id+"F5.imprint","IMPRINT",EDGE,{"disambiguationData":[TD([[subQ3,-1.0]])],"derivedFrom":subQ0}),makeQuery(id+"F5.imprint","IMPRINT",EDGE,{"disambiguationData":[TD([[makeQuery(id+"F5.imprint","INTERSECT",VERTEX,{"derivedFrom":[subQ0,sQuery(id+"F5.wireOp",EDGE,"E46")]}),1.0]])],"derivedFrom":subQ0})])],"isStart":false});}
            var Q3;
            {var subQ0=sQuery(id+"F5.wireOp",EDGE,"E28.top");var subQ1=sQuery(id+"F5.wireOp",EDGE,"E31");var subQ3=makeQuery(id+"F5.imprint","INTERSECT",VERTEX,{"disambiguationData":[OD(0.0)],"derivedFrom":[subQ0,subQ1]});Q3=makeQuery(id+"F9.opExtrude","CAP_EDGE",EDGE,{"disambiguationData":[OSD([subQ0]),TDD([makeQuery(id+"F5.imprint","IMPRINT",EDGE,{"disambiguationData":[TD([[makeQuery(id+"F5.imprint","INTERSECT",VERTEX,{"derivedFrom":[subQ0,sQuery(id+"F5.wireOp",EDGE,"E45")]}),-1.0]])],"derivedFrom":subQ0}),makeQuery(id+"F5.imprint","IMPRINT",EDGE,{"disambiguationData":[TD([[subQ3,-1.0]])],"derivedFrom":subQ0}),makeQuery(id+"F5.imprint","IMPRINT",EDGE,{"disambiguationData":[TD([[makeQuery(id+"F5.imprint","INTERSECT",VERTEX,{"derivedFrom":[subQ0,sQuery(id+"F5.wireOp",EDGE,"E46")]}),1.0]])],"derivedFrom":subQ0})])],"isStart":false});}
            var Q4;
            {var subQ0=sQuery(id+"F5.wireOp",EDGE,"E28.top");Q4=makeQuery(id+"F8.opExtrude","CAP_EDGE",EDGE,{"disambiguationData":[OSD([subQ0]),TDD([makeQuery(id+"F5.imprint","IMPRINT",EDGE,{"disambiguationData":[TD([[makeQuery(id+"F5.imprint","INTERSECT",VERTEX,{"derivedFrom":[subQ0,sQuery(id+"F5.wireOp",EDGE,"E46")]}),-1.0]])],"derivedFrom":subQ0})])],"isStart":false});}
            var Q5;
            {var subQ0=sQuery(id+"F5.wireOp",EDGE,"E28.bottom");Q5=makeQuery(id+"F8.opExtrude","CAP_EDGE",EDGE,{"disambiguationData":[OSD([subQ0]),TDD([makeQuery(id+"F5.imprint","IMPRINT",EDGE,{"disambiguationData":[TD([[makeQuery(id+"F5.imprint","INTERSECT",VERTEX,{"derivedFrom":[subQ0,sQuery(id+"F5.wireOp",EDGE,"E46")]}),-1.0]])],"derivedFrom":subQ0})])],"isStart":false});}
            var Q6;
            {var subQ0=sQuery(id+"F5.wireOp",EDGE,"E28.bottom");Q6=makeQuery(id+"F8.opExtrude","CAP_EDGE",EDGE,{"disambiguationData":[OSD([subQ0]),TDD([makeQuery(id+"F5.imprint","IMPRINT",EDGE,{"disambiguationData":[TD([[makeQuery(id+"F5.imprint","INTERSECT",VERTEX,{"derivedFrom":[subQ0,sQuery(id+"F5.wireOp",EDGE,"E34.5")]}),-1.0]])],"derivedFrom":subQ0})])],"isStart":false});}
            var Q7;
            {var subQ0=sQuery(id+"F5.wireOp",EDGE,"E28.top");Q7=makeQuery(id+"F8.opExtrude","CAP_EDGE",EDGE,{"disambiguationData":[OSD([subQ0]),TDD([makeQuery(id+"F5.imprint","IMPRINT",EDGE,{"disambiguationData":[TD([[makeQuery(id+"F5.imprint","INTERSECT",VERTEX,{"derivedFrom":[subQ0,sQuery(id+"F5.wireOp",EDGE,"E34.0")]}),-1.0]])],"derivedFrom":subQ0})])],"isStart":false});}
            var Q8;
            {var subQ0=sQuery(id+"F5.wireOp",EDGE,"E28.top");Q8=makeQuery(id+"F8.opExtrude","CAP_EDGE",EDGE,{"disambiguationData":[OSD([subQ0]),TDD([makeQuery(id+"F5.imprint","IMPRINT",EDGE,{"disambiguationData":[TD([[makeQuery(id+"F5.imprint","INTERSECT",VERTEX,{"derivedFrom":[subQ0,sQuery(id+"F5.wireOp",EDGE,"E35.0")]}),-1.0]])],"derivedFrom":subQ0})])],"isStart":false});}
            var Q9;
            {var subQ0=sQuery(id+"F5.wireOp",EDGE,"E28.bottom");Q9=makeQuery(id+"F8.opExtrude","CAP_EDGE",EDGE,{"disambiguationData":[OSD([subQ0]),TDD([makeQuery(id+"F5.imprint","IMPRINT",EDGE,{"disambiguationData":[TD([[makeQuery(id+"F5.imprint","INTERSECT",VERTEX,{"derivedFrom":[subQ0,sQuery(id+"F5.wireOp",EDGE,"E35.5")]}),-1.0]])],"derivedFrom":subQ0})])],"isStart":false});}
            var Q10;
            {var subQ0=sQuery(id+"F5.wireOp",EDGE,"E28.bottom");Q10=makeQuery(id+"F8.opExtrude","CAP_EDGE",EDGE,{"disambiguationData":[OSD([subQ0]),TDD([makeQuery(id+"F5.imprint","IMPRINT",EDGE,{"disambiguationData":[TD([[makeQuery(id+"F5.imprint","INTERSECT",VERTEX,{"derivedFrom":[subQ0,sQuery(id+"F5.wireOp",EDGE,"E36.5")]}),-1.0]])],"derivedFrom":subQ0})])],"isStart":false});}
            var Q11;
            {var subQ0=sQuery(id+"F5.wireOp",EDGE,"E28.top");Q11=makeQuery(id+"F8.opExtrude","CAP_EDGE",EDGE,{"disambiguationData":[OSD([subQ0]),TDD([makeQuery(id+"F5.imprint","IMPRINT",EDGE,{"disambiguationData":[TD([[makeQuery(id+"F5.imprint","INTERSECT",VERTEX,{"derivedFrom":[subQ0,sQuery(id+"F5.wireOp",EDGE,"E36.0")]}),-1.0]])],"derivedFrom":subQ0})])],"isStart":false});}
            var Q12;
            {var subQ0=sQuery(id+"F5.wireOp",EDGE,"E28.top");Q12=makeQuery(id+"F8.opExtrude","CAP_EDGE",EDGE,{"disambiguationData":[OSD([subQ0]),TDD([makeQuery(id+"F5.imprint","IMPRINT",EDGE,{"disambiguationData":[TD([[makeQuery(id+"F5.imprint","INTERSECT",VERTEX,{"derivedFrom":[subQ0,sQuery(id+"F5.wireOp",EDGE,"E48")]}),1.0]])],"derivedFrom":subQ0})])],"isStart":false});}
            var Q13;
            {var subQ0=sQuery(id+"F5.wireOp",EDGE,"E28.bottom");Q13=makeQuery(id+"F8.opExtrude","CAP_EDGE",EDGE,{"disambiguationData":[OSD([subQ0]),TDD([makeQuery(id+"F5.imprint","IMPRINT",EDGE,{"disambiguationData":[TD([[makeQuery(id+"F5.imprint","INTERSECT",VERTEX,{"derivedFrom":[subQ0,sQuery(id+"F5.wireOp",EDGE,"E48")]}),1.0]])],"derivedFrom":subQ0})])],"isStart":false});}
            var Q14;
            {var subQ0=sQuery(id+"F5.wireOp",EDGE,"E28.bottom");var subQ1=sQuery(id+"F5.wireOp",EDGE,"E33");var subQ3=makeQuery(id+"F5.imprint","INTERSECT",VERTEX,{"disambiguationData":[OD(0.0)],"derivedFrom":[subQ0,subQ1]});Q14=makeQuery(id+"F9.opExtrude","CAP_EDGE",EDGE,{"disambiguationData":[OSD([subQ0]),TDD([makeQuery(id+"F5.imprint","IMPRINT",EDGE,{"disambiguationData":[TD([[makeQuery(id+"F5.imprint","INTERSECT",VERTEX,{"derivedFrom":[subQ0,sQuery(id+"F5.wireOp",EDGE,"E48")]}),-1.0]])],"derivedFrom":subQ0}),makeQuery(id+"F5.imprint","IMPRINT",EDGE,{"disambiguationData":[TD([[subQ3,-1.0]])],"derivedFrom":subQ0}),makeQuery(id+"F5.imprint","IMPRINT",EDGE,{"disambiguationData":[TD([[makeQuery(id+"F5.imprint","INTERSECT",VERTEX,{"derivedFrom":[subQ0,sQuery(id+"F5.wireOp",EDGE,"E47")]}),1.0]])],"derivedFrom":subQ0})])],"isStart":false});}
            var Q15;
            {var subQ0=sQuery(id+"F5.wireOp",EDGE,"E28.top");var subQ1=sQuery(id+"F5.wireOp",EDGE,"E33");var subQ3=makeQuery(id+"F5.imprint","INTERSECT",VERTEX,{"disambiguationData":[OD(0.0)],"derivedFrom":[subQ0,subQ1]});Q15=makeQuery(id+"F9.opExtrude","CAP_EDGE",EDGE,{"disambiguationData":[OSD([subQ0]),TDD([makeQuery(id+"F5.imprint","IMPRINT",EDGE,{"disambiguationData":[TD([[makeQuery(id+"F5.imprint","INTERSECT",VERTEX,{"derivedFrom":[subQ0,sQuery(id+"F5.wireOp",EDGE,"E48")]}),-1.0]])],"derivedFrom":subQ0}),makeQuery(id+"F5.imprint","IMPRINT",EDGE,{"disambiguationData":[TD([[subQ3,-1.0]])],"derivedFrom":subQ0}),makeQuery(id+"F5.imprint","IMPRINT",EDGE,{"disambiguationData":[TD([[makeQuery(id+"F5.imprint","INTERSECT",VERTEX,{"derivedFrom":[subQ0,sQuery(id+"F5.wireOp",EDGE,"E47")]}),1.0]])],"derivedFrom":subQ0})])],"isStart":false});}
            var Q16;
            {var subQ0=sQuery(id+"F5.wireOp",EDGE,"E28.top");Q16=makeQuery(id+"F8.opExtrude","CAP_EDGE",EDGE,{"disambiguationData":[OSD([subQ0]),TDD([makeQuery(id+"F5.imprint","IMPRINT",EDGE,{"disambiguationData":[TD([[makeQuery(id+"F5.imprint","INTERSECT",VERTEX,{"derivedFrom":[subQ0,sQuery(id+"F5.wireOp",EDGE,"E47")]}),-1.0]])],"derivedFrom":subQ0})])],"isStart":false});}
            var Q17;
            {var subQ0=sQuery(id+"F5.wireOp",EDGE,"E28.bottom");Q17=makeQuery(id+"F8.opExtrude","CAP_EDGE",EDGE,{"disambiguationData":[OSD([subQ0]),TDD([makeQuery(id+"F5.imprint","IMPRINT",EDGE,{"disambiguationData":[TD([[makeQuery(id+"F5.imprint","INTERSECT",VERTEX,{"derivedFrom":[subQ0,sQuery(id+"F5.wireOp",EDGE,"E47")]}),-1.0]])],"derivedFrom":subQ0})])],"isStart":false});}
            var Q18;
            Q18=makeQuery(id+"F8.opExtrude","CAP_EDGE",EDGE,{"disambiguationData":[OSD([sQuery(id+"F5.wireOp",EDGE,"E45")])],"isStart":false});
            var Q19;
            Q19=makeQuery(id+"F8.opExtrude","CAP_EDGE",EDGE,{"disambiguationData":[OSD([sQuery(id+"F5.wireOp",EDGE,"E46")])],"isStart":false});
            var Q20;
            Q20=makeQuery(id+"F8.opExtrude","CAP_EDGE",EDGE,{"disambiguationData":[OSD([sQuery(id+"F5.wireOp",EDGE,"E48")])],"isStart":false});
            var Q21;
            Q21=makeQuery(id+"F8.opExtrude","CAP_EDGE",EDGE,{"disambiguationData":[OSD([sQuery(id+"F5.wireOp",EDGE,"E47")])],"isStart":false});
            chamfer(context, id + "F10", {"entities" : qUnion([Q0, Q1, Q2, Q3, Q4, Q5, Q6, Q7, Q8, Q9, Q10, Q11, Q12, Q13, Q14, Q15, Q16, Q17, Q18, Q19, Q20, Q21]), "width" : 1 * mm});
        }
        {
            var Q0;
            Q0=makeQuery(id+"F1.opExtrude","SWEPT_EDGE",EDGE,{"disambiguationData":[OSD([sQuery(id+"F0.wireOp",EDGE,"E13.1"),sQuery(id+"F0.wireOp",EDGE,"E13.2")])]});
            var Q1;
            Q1=makeQuery(id+"F1.opExtrude","SWEPT_EDGE",EDGE,{"disambiguationData":[OSD([sQuery(id+"F0.wireOp",EDGE,"E13.2"),sQuery(id+"F0.wireOp",EDGE,"E13.3")])]});
            var Q2;
            Q2=makeQuery(id+"F1.opExtrude","SWEPT_EDGE",EDGE,{"disambiguationData":[OSD([sQuery(id+"F0.wireOp",EDGE,"E13.0"),sQuery(id+"F0.wireOp",EDGE,"E13.1")])]});
            var Q3;
            Q3=makeQuery(id+"F1.opExtrude","SWEPT_EDGE",EDGE,{"disambiguationData":[OSD([sQuery(id+"F0.wireOp",EDGE,"E13.0"),sQuery(id+"F0.wireOp",EDGE,"E13.3")])]});
            var Q4;
            Q4=makeQuery(id+"F2.opExtrude","SWEPT_EDGE",EDGE,{"disambiguationData":[OSD([sQuery(id+"F0.wireOp",EDGE,"E9.2"),sQuery(id+"F0.wireOp",EDGE,"E9.3")])]});
            var Q5;
            {var subQ0=sQuery(id+"F0.wireOp",EDGE,"E11.2");var subQ1=sQuery(id+"F0.wireOp",EDGE,"E9.3");Q5=makeQuery(id+"F4.boolean.opBoolean","MERGE",EDGE,{"derivedFrom":[makeQuery(id+"F1.opExtrude","SWEPT_EDGE",EDGE,{"disambiguationData":[OSD([subQ1,subQ0])]}),makeQuery(id+"F2.opExtrude","SWEPT_EDGE",EDGE,{"disambiguationData":[OSD([subQ1,subQ0])]})]});}
            var Q6;
            Q6=makeQuery(id+"F2.opExtrude","SWEPT_EDGE",EDGE,{"disambiguationData":[OSD([sQuery(id+"F0.wireOp",EDGE,"E9.1"),sQuery(id+"F0.wireOp",EDGE,"E9.2")])]});
            var Q7;
            {var subQ0=sQuery(id+"F0.wireOp",EDGE,"E11.2");var subQ1=sQuery(id+"F0.wireOp",EDGE,"E9.1");Q7=makeQuery(id+"F2.boolean.opBoolean","MERGE",EDGE,{"derivedFrom":[makeQuery(id+"F1.opExtrude","SWEPT_EDGE",EDGE,{"disambiguationData":[OSD([subQ1,subQ0])]}),makeQuery(id+"F2.opExtrude","SWEPT_EDGE",EDGE,{"disambiguationData":[OSD([subQ1,subQ0])]})]});}
            var Q8;
            {var subQ0=sQuery(id+"F0.wireOp",EDGE,"E11.1");var subQ1=sQuery(id+"F0.wireOp",EDGE,"E9.2");Q8=makeQuery(id+"F2.boolean.opBoolean","MERGE",EDGE,{"derivedFrom":[makeQuery(id+"F1.opExtrude","SWEPT_EDGE",EDGE,{"disambiguationData":[OSD([subQ1,subQ0])]}),makeQuery(id+"F2.opExtrude","SWEPT_EDGE",EDGE,{"disambiguationData":[OSD([subQ1,subQ0])]})]});}
            var Q9;
            {var subQ0=sQuery(id+"F0.wireOp",EDGE,"E10.2");var subQ1=sQuery(id+"F0.wireOp",EDGE,"E9.1");Q9=makeQuery(id+"F2.boolean.opBoolean","MERGE",EDGE,{"derivedFrom":[makeQuery(id+"F1.opExtrude","SWEPT_EDGE",EDGE,{"disambiguationData":[OSD([subQ1,subQ0])]}),makeQuery(id+"F2.opExtrude","SWEPT_EDGE",EDGE,{"disambiguationData":[OSD([subQ1,subQ0])]})]});}
            var Q10;
            {var subQ0=sQuery(id+"F0.wireOp",EDGE,"E21");var subQ1=sQuery(id+"F0.wireOp",EDGE,"E11.1");Q10=makeQuery(id+"F2.boolean.opBoolean","MERGE",EDGE,{"derivedFrom":[makeQuery(id+"F1.opExtrude","SWEPT_EDGE",EDGE,{"disambiguationData":[OSD([subQ1,subQ0])]}),makeQuery(id+"F2.opExtrude","SWEPT_EDGE",EDGE,{"disambiguationData":[OSD([subQ1,subQ0])]})]});}
            var Q11;
            {var subQ0=sQuery(id+"F0.wireOp",EDGE,"E23");var subQ1=sQuery(id+"F0.wireOp",EDGE,"E10.2");Q11=makeQuery(id+"F2.boolean.opBoolean","MERGE",EDGE,{"derivedFrom":[makeQuery(id+"F1.opExtrude","SWEPT_EDGE",EDGE,{"disambiguationData":[OSD([subQ1,subQ0])]}),makeQuery(id+"F2.opExtrude","SWEPT_EDGE",EDGE,{"disambiguationData":[OSD([subQ1,subQ0])]})]});}
            var Q12;
            {var subQ0=sQuery(id+"F0.wireOp",EDGE,"E10.2");var subQ1=sQuery(id+"F0.wireOp",EDGE,"E9.3");Q12=makeQuery(id+"F4.boolean.opBoolean","MERGE",EDGE,{"derivedFrom":[makeQuery(id+"F1.opExtrude","SWEPT_EDGE",EDGE,{"disambiguationData":[OSD([subQ1,subQ0])]}),makeQuery(id+"F2.opExtrude","SWEPT_EDGE",EDGE,{"disambiguationData":[OSD([subQ1,subQ0])]})]});}
            var Q13;
            {var subQ0=sQuery(id+"F0.wireOp",EDGE,"E22");var subQ1=sQuery(id+"F0.wireOp",EDGE,"E10.2");Q13=makeQuery(id+"F2.boolean.opBoolean","MERGE",EDGE,{"derivedFrom":[makeQuery(id+"F1.opExtrude","SWEPT_EDGE",EDGE,{"disambiguationData":[OSD([subQ1,subQ0])]}),makeQuery(id+"F2.opExtrude","SWEPT_EDGE",EDGE,{"disambiguationData":[OSD([subQ1,subQ0])]})]});}
            var Q14;
            {var subQ0=sQuery(id+"F0.wireOp",EDGE,"E22");var subQ1=sQuery(id+"F0.wireOp",EDGE,"E11.2");Q14=makeQuery(id+"F2.boolean.opBoolean","MERGE",EDGE,{"derivedFrom":[makeQuery(id+"F1.opExtrude","SWEPT_EDGE",EDGE,{"disambiguationData":[OSD([subQ1,subQ0])]}),makeQuery(id+"F2.opExtrude","SWEPT_EDGE",EDGE,{"disambiguationData":[OSD([subQ1,subQ0])]})]});}
            var Q15;
            {var subQ0=sQuery(id+"F0.wireOp",EDGE,"E10.1");var subQ1=sQuery(id+"F0.wireOp",EDGE,"E9.2");Q15=makeQuery(id+"F2.boolean.opBoolean","MERGE",EDGE,{"derivedFrom":[makeQuery(id+"F1.opExtrude","SWEPT_EDGE",EDGE,{"disambiguationData":[OSD([subQ1,subQ0])]}),makeQuery(id+"F2.opExtrude","SWEPT_EDGE",EDGE,{"disambiguationData":[OSD([subQ1,subQ0])]})]});}
            var Q16;
            {var subQ0=sQuery(id+"F0.wireOp",EDGE,"E21");var subQ1=sQuery(id+"F0.wireOp",EDGE,"E10.1");Q16=makeQuery(id+"F2.boolean.opBoolean","MERGE",EDGE,{"derivedFrom":[makeQuery(id+"F1.opExtrude","SWEPT_EDGE",EDGE,{"disambiguationData":[OSD([subQ1,subQ0])]}),makeQuery(id+"F2.opExtrude","SWEPT_EDGE",EDGE,{"disambiguationData":[OSD([subQ1,subQ0])]})]});}
            var Q17;
            {var subQ0=sQuery(id+"F0.wireOp",EDGE,"E20");var subQ1=sQuery(id+"F0.wireOp",EDGE,"E11.1");Q17=makeQuery(id+"F2.boolean.opBoolean","MERGE",EDGE,{"derivedFrom":[makeQuery(id+"F1.opExtrude","SWEPT_EDGE",EDGE,{"disambiguationData":[OSD([subQ1,subQ0])]}),makeQuery(id+"F2.opExtrude","SWEPT_EDGE",EDGE,{"disambiguationData":[OSD([subQ1,subQ0])]})]});}
            var Q18;
            {var subQ0=sQuery(id+"F0.wireOp",EDGE,"E10.0");var subQ1=sQuery(id+"F0.wireOp",EDGE,"E9.1");Q18=makeQuery(id+"F2.boolean.opBoolean","MERGE",EDGE,{"derivedFrom":[makeQuery(id+"F1.opExtrude","SWEPT_EDGE",EDGE,{"disambiguationData":[OSD([subQ1,subQ0])]}),makeQuery(id+"F2.opExtrude","SWEPT_EDGE",EDGE,{"disambiguationData":[OSD([subQ1,subQ0])]})]});}
            var Q19;
            {var subQ0=sQuery(id+"F0.wireOp",EDGE,"E19");var subQ1=sQuery(id+"F0.wireOp",EDGE,"E10.0");Q19=makeQuery(id+"F2.boolean.opBoolean","MERGE",EDGE,{"derivedFrom":[makeQuery(id+"F1.opExtrude","SWEPT_EDGE",EDGE,{"disambiguationData":[OSD([subQ1,subQ0])]}),makeQuery(id+"F2.opExtrude","SWEPT_EDGE",EDGE,{"disambiguationData":[OSD([subQ1,subQ0])]})]});}
            var Q20;
            {var subQ0=sQuery(id+"F0.wireOp",EDGE,"E19");var subQ1=sQuery(id+"F0.wireOp",EDGE,"E11.0");Q20=makeQuery(id+"F2.boolean.opBoolean","MERGE",EDGE,{"derivedFrom":[makeQuery(id+"F1.opExtrude","SWEPT_EDGE",EDGE,{"disambiguationData":[OSD([subQ1,subQ0])]}),makeQuery(id+"F2.opExtrude","SWEPT_EDGE",EDGE,{"disambiguationData":[OSD([subQ1,subQ0])]})]});}
            var Q21;
            {var subQ0=sQuery(id+"F0.wireOp",EDGE,"E11.0");var subQ1=sQuery(id+"F0.wireOp",EDGE,"E9.1");Q21=makeQuery(id+"F2.boolean.opBoolean","MERGE",EDGE,{"derivedFrom":[makeQuery(id+"F1.opExtrude","SWEPT_EDGE",EDGE,{"disambiguationData":[OSD([subQ1,subQ0])]}),makeQuery(id+"F2.opExtrude","SWEPT_EDGE",EDGE,{"disambiguationData":[OSD([subQ1,subQ0])]})]});}
            var Q22;
            {var subQ0=sQuery(id+"F0.wireOp",EDGE,"E11.1");var subQ1=sQuery(id+"F0.wireOp",EDGE,"E9.0");Q22=makeQuery(id+"F2.boolean.opBoolean","MERGE",EDGE,{"derivedFrom":[makeQuery(id+"F1.opExtrude","SWEPT_EDGE",EDGE,{"disambiguationData":[OSD([subQ1,subQ0])]}),makeQuery(id+"F2.opExtrude","SWEPT_EDGE",EDGE,{"disambiguationData":[OSD([subQ1,subQ0])]})]});}
            var Q23;
            {var subQ0=sQuery(id+"F0.wireOp",EDGE,"E10.1");var subQ1=sQuery(id+"F0.wireOp",EDGE,"E9.0");Q23=makeQuery(id+"F2.boolean.opBoolean","MERGE",EDGE,{"derivedFrom":[makeQuery(id+"F1.opExtrude","SWEPT_EDGE",EDGE,{"disambiguationData":[OSD([subQ1,subQ0])]}),makeQuery(id+"F2.opExtrude","SWEPT_EDGE",EDGE,{"disambiguationData":[OSD([subQ1,subQ0])]})]});}
            var Q24;
            {var subQ0=sQuery(id+"F0.wireOp",EDGE,"E11.0");var subQ1=sQuery(id+"F0.wireOp",EDGE,"E9.3");Q24=makeQuery(id+"F4.boolean.opBoolean","MERGE",EDGE,{"derivedFrom":[makeQuery(id+"F1.opExtrude","SWEPT_EDGE",EDGE,{"disambiguationData":[OSD([subQ1,subQ0])]}),makeQuery(id+"F2.opExtrude","SWEPT_EDGE",EDGE,{"disambiguationData":[OSD([subQ1,subQ0])]})]});}
            var Q25;
            {var subQ0=sQuery(id+"F0.wireOp",EDGE,"E18");var subQ1=sQuery(id+"F0.wireOp",EDGE,"E11.0");Q25=makeQuery(id+"F2.boolean.opBoolean","MERGE",EDGE,{"derivedFrom":[makeQuery(id+"F1.opExtrude","SWEPT_EDGE",EDGE,{"disambiguationData":[OSD([subQ1,subQ0])]}),makeQuery(id+"F2.opExtrude","SWEPT_EDGE",EDGE,{"disambiguationData":[OSD([subQ1,subQ0])]})]});}
            var Q26;
            {var subQ0=sQuery(id+"F0.wireOp",EDGE,"E18");var subQ1=sQuery(id+"F0.wireOp",EDGE,"E10.0");Q26=makeQuery(id+"F2.boolean.opBoolean","MERGE",EDGE,{"derivedFrom":[makeQuery(id+"F1.opExtrude","SWEPT_EDGE",EDGE,{"disambiguationData":[OSD([subQ1,subQ0])]}),makeQuery(id+"F2.opExtrude","SWEPT_EDGE",EDGE,{"disambiguationData":[OSD([subQ1,subQ0])]})]});}
            var Q27;
            {var subQ0=sQuery(id+"F0.wireOp",EDGE,"E10.0");var subQ1=sQuery(id+"F0.wireOp",EDGE,"E9.3");Q27=makeQuery(id+"F4.boolean.opBoolean","MERGE",EDGE,{"derivedFrom":[makeQuery(id+"F1.opExtrude","SWEPT_EDGE",EDGE,{"disambiguationData":[OSD([subQ1,subQ0])]}),makeQuery(id+"F2.opExtrude","SWEPT_EDGE",EDGE,{"disambiguationData":[OSD([subQ1,subQ0])]})]});}
            var Q28;
            {var subQ0=sQuery(id+"F0.wireOp",EDGE,"E20");var subQ1=sQuery(id+"F0.wireOp",EDGE,"E10.1");Q28=makeQuery(id+"F2.boolean.opBoolean","MERGE",EDGE,{"derivedFrom":[makeQuery(id+"F1.opExtrude","SWEPT_EDGE",EDGE,{"disambiguationData":[OSD([subQ1,subQ0])]}),makeQuery(id+"F2.opExtrude","SWEPT_EDGE",EDGE,{"disambiguationData":[OSD([subQ1,subQ0])]})]});}
            var Q29;
            Q29=makeQuery(id+"F2.opExtrude","SWEPT_EDGE",EDGE,{"disambiguationData":[OSD([sQuery(id+"F0.wireOp",EDGE,"E9.0"),sQuery(id+"F0.wireOp",EDGE,"E9.1")])]});
            var Q30;
            Q30=makeQuery(id+"F2.opExtrude","SWEPT_EDGE",EDGE,{"disambiguationData":[OSD([sQuery(id+"F0.wireOp",EDGE,"E9.0"),sQuery(id+"F0.wireOp",EDGE,"E9.3")])]});
            var Q31;
            {var subQ0=sQuery(id+"F0.wireOp",EDGE,"E12.2");var subQ1=sQuery(id+"F0.wireOp",EDGE,"E10.1");Q31=makeQuery(id+"F2.boolean.opBoolean","MERGE",EDGE,{"derivedFrom":[makeQuery(id+"F1.opExtrude","SWEPT_EDGE",EDGE,{"disambiguationData":[OSD([subQ1,subQ0])]}),makeQuery(id+"F2.opExtrude","SWEPT_EDGE",EDGE,{"disambiguationData":[OSD([subQ1,subQ0])]})]});}
            var Q32;
            {var subQ0=sQuery(id+"F0.wireOp",EDGE,"E12.1");var subQ1=sQuery(id+"F0.wireOp",EDGE,"E10.2");Q32=makeQuery(id+"F2.boolean.opBoolean","MERGE",EDGE,{"derivedFrom":[makeQuery(id+"F1.opExtrude","SWEPT_EDGE",EDGE,{"disambiguationData":[OSD([subQ1,subQ0])]}),makeQuery(id+"F2.opExtrude","SWEPT_EDGE",EDGE,{"disambiguationData":[OSD([subQ1,subQ0])]})]});}
            var Q33;
            {var subQ0=sQuery(id+"F0.wireOp",EDGE,"E10.2");var subQ1=sQuery(id+"F0.wireOp",EDGE,"E10.1");Q33=makeQuery(id+"F2.boolean.opBoolean","MERGE",EDGE,{"derivedFrom":[makeQuery(id+"F1.opExtrude","SWEPT_EDGE",EDGE,{"disambiguationData":[OSD([subQ1,subQ0])]}),makeQuery(id+"F2.opExtrude","SWEPT_EDGE",EDGE,{"disambiguationData":[OSD([subQ1,subQ0])]})]});}
            var Q34;
            {var subQ0=sQuery(id+"F0.wireOp",EDGE,"E12.2");var subQ1=sQuery(id+"F0.wireOp",EDGE,"E9.3");Q34=makeQuery(id+"F4.boolean.opBoolean","MERGE",EDGE,{"derivedFrom":[makeQuery(id+"F1.opExtrude","SWEPT_EDGE",EDGE,{"disambiguationData":[OSD([subQ1,subQ0])]}),makeQuery(id+"F2.opExtrude","SWEPT_EDGE",EDGE,{"disambiguationData":[OSD([subQ1,subQ0])]})]});}
            var Q35;
            {var subQ0=sQuery(id+"F0.wireOp",EDGE,"E12.1");var subQ1=sQuery(id+"F0.wireOp",EDGE,"E10.0");Q35=makeQuery(id+"F2.boolean.opBoolean","MERGE",EDGE,{"derivedFrom":[makeQuery(id+"F1.opExtrude","SWEPT_EDGE",EDGE,{"disambiguationData":[OSD([subQ1,subQ0])]}),makeQuery(id+"F2.opExtrude","SWEPT_EDGE",EDGE,{"disambiguationData":[OSD([subQ1,subQ0])]})]});}
            var Q36;
            {var subQ0=sQuery(id+"F0.wireOp",EDGE,"E10.1");var subQ1=sQuery(id+"F0.wireOp",EDGE,"E10.0");Q36=makeQuery(id+"F2.boolean.opBoolean","MERGE",EDGE,{"derivedFrom":[makeQuery(id+"F1.opExtrude","SWEPT_EDGE",EDGE,{"disambiguationData":[OSD([subQ1,subQ0])]}),makeQuery(id+"F2.opExtrude","SWEPT_EDGE",EDGE,{"disambiguationData":[OSD([subQ1,subQ0])]})]});}
            var Q37;
            {var subQ0=sQuery(id+"F0.wireOp",EDGE,"E12.0");var subQ1=sQuery(id+"F0.wireOp",EDGE,"E10.1");Q37=makeQuery(id+"F2.boolean.opBoolean","MERGE",EDGE,{"derivedFrom":[makeQuery(id+"F1.opExtrude","SWEPT_EDGE",EDGE,{"disambiguationData":[OSD([subQ1,subQ0])]}),makeQuery(id+"F2.opExtrude","SWEPT_EDGE",EDGE,{"disambiguationData":[OSD([subQ1,subQ0])]})]});}
            var Q38;
            {var subQ0=sQuery(id+"F0.wireOp",EDGE,"E12.0");var subQ1=sQuery(id+"F0.wireOp",EDGE,"E9.3");Q38=makeQuery(id+"F4.boolean.opBoolean","MERGE",EDGE,{"derivedFrom":[makeQuery(id+"F1.opExtrude","SWEPT_EDGE",EDGE,{"disambiguationData":[OSD([subQ1,subQ0])]}),makeQuery(id+"F2.opExtrude","SWEPT_EDGE",EDGE,{"disambiguationData":[OSD([subQ1,subQ0])]})]});}
            var Q39;
            {var subQ0=sQuery(id+"F0.wireOp",EDGE,"E23");var subQ1=sQuery(id+"F0.wireOp",EDGE,"E11.2");Q39=makeQuery(id+"F2.boolean.opBoolean","MERGE",EDGE,{"derivedFrom":[makeQuery(id+"F1.opExtrude","SWEPT_EDGE",EDGE,{"disambiguationData":[OSD([subQ1,subQ0])]}),makeQuery(id+"F2.opExtrude","SWEPT_EDGE",EDGE,{"disambiguationData":[OSD([subQ1,subQ0])]})]});}
            chamfer(context, id + "F11", {"entities" : qUnion([Q0, Q1, Q2, Q3, Q4, Q5, Q6, Q7, Q8, Q9, Q10, Q11, Q12, Q13, Q14, Q15, Q16, Q17, Q18, Q19, Q20, Q21, Q22, Q23, Q24, Q25, Q26, Q27, Q28, Q29, Q30, Q31, Q32, Q33, Q34, Q35, Q36, Q37, Q38, Q39]), "width" : 2 * mm});
        }
        {
            var Q0;
            Q0=makeQuery(id+"F1.opExtrude","CAP_FACE",FACE,{"disambiguationData":[OSD([sQuery(id+"F0.wireOp",EDGE,"E1"),sQuery(id+"F0.wireOp",EDGE,"E2"),sQuery(id+"F0.wireOp",EDGE,"E3"),sQuery(id+"F0.wireOp",EDGE,"E4"),sQuery(id+"F0.wireOp",EDGE,"E9.0"),sQuery(id+"F0.wireOp",EDGE,"E9.1"),sQuery(id+"F0.wireOp",EDGE,"E9.2"),sQuery(id+"F0.wireOp",EDGE,"E9.3"),sQuery(id+"F0.wireOp",EDGE,"E10.0"),sQuery(id+"F0.wireOp",EDGE,"E10.1"),sQuery(id+"F0.wireOp",EDGE,"E10.2"),sQuery(id+"F0.wireOp",EDGE,"E11.0"),sQuery(id+"F0.wireOp",EDGE,"E11.1"),sQuery(id+"F0.wireOp",EDGE,"E11.2"),sQuery(id+"F0.wireOp",EDGE,"E12.0"),sQuery(id+"F0.wireOp",EDGE,"E12.1"),sQuery(id+"F0.wireOp",EDGE,"E12.2"),sQuery(id+"F0.wireOp",EDGE,"E13.0"),sQuery(id+"F0.wireOp",EDGE,"E13.1"),sQuery(id+"F0.wireOp",EDGE,"E13.2"),sQuery(id+"F0.wireOp",EDGE,"E13.3"),sQuery(id+"F0.wireOp",EDGE,"E14"),sQuery(id+"F0.wireOp",EDGE,"E15"),sQuery(id+"F0.wireOp",EDGE,"E16"),sQuery(id+"F0.wireOp",EDGE,"E18"),sQuery(id+"F0.wireOp",EDGE,"E19"),sQuery(id+"F0.wireOp",EDGE,"E20"),sQuery(id+"F0.wireOp",EDGE,"E21"),sQuery(id+"F0.wireOp",EDGE,"E22"),sQuery(id+"F0.wireOp",EDGE,"E23")])],"isStart":false});
            var sketch = newSketch(context, id + "F12", { "sketchPlane" : qUnion([Q0])});
            skLineSegment(sketch, "E51.bottom", {"start": v(-83.5, 44.5) * mm, "end": v(-76, 44.5) * mm});
            skLineSegment(sketch, "E51.top", {"start": v(-83.5, 48.5) * mm, "end": v(-76, 48.5) * mm});
            skLineSegment(sketch, "E51.left", {"start": v(-83.5, 44.5) * mm, "end": v(-83.5, 48.5) * mm});
            skLineSegment(sketch, "E51.right", {"start": v(-76, 44.5) * mm, "end": v(-76, 48.5) * mm});
            skLineSegment(sketch, "E52.bottom", {"start": v(-61, 44.5) * mm, "end": v(-50.44, 44.5) * mm});
            skLineSegment(sketch, "E52.top", {"start": v(-61, 48.5) * mm, "end": v(-50.44, 48.5) * mm});
            skLineSegment(sketch, "E52.left", {"start": v(-61, 44.5) * mm, "end": v(-61, 48.5) * mm});
            skLineSegment(sketch, "E52.right", {"start": v(-50.44, 44.5) * mm, "end": v(-50.44, 48.5) * mm});
            skLineSegment(sketch, "E53.bottom", {"start": v(-35.06, 44.5) * mm, "end": v(-21.94, 44.5) * mm});
            skLineSegment(sketch, "E53.top", {"start": v(-35.06, 48.5) * mm, "end": v(-21.94, 48.5) * mm});
            skLineSegment(sketch, "E53.left", {"start": v(-35.06, 44.5) * mm, "end": v(-35.06, 48.5) * mm});
            skLineSegment(sketch, "E53.right", {"start": v(-21.94, 44.5) * mm, "end": v(-21.94, 48.5) * mm});
            skLineSegment(sketch, "E54.bottom", {"start": v(-6.56, 44.5) * mm, "end": v(6.56, 44.5) * mm});
            skLineSegment(sketch, "E54.top", {"start": v(-6.56, 48.5) * mm, "end": v(6.56, 48.5) * mm});
            skLineSegment(sketch, "E54.left", {"start": v(-6.56, 44.5) * mm, "end": v(-6.56, 48.5) * mm});
            skLineSegment(sketch, "E54.right", {"start": v(6.56, 44.5) * mm, "end": v(6.56, 48.5) * mm});
            skLineSegment(sketch, "E55.bottom", {"start": v(21.94, 44.5) * mm, "end": v(35.06, 44.5) * mm});
            skLineSegment(sketch, "E55.top", {"start": v(21.94, 48.5) * mm, "end": v(35.06, 48.5) * mm});
            skLineSegment(sketch, "E55.left", {"start": v(21.94, 44.5) * mm, "end": v(21.94, 48.5) * mm});
            skLineSegment(sketch, "E55.right", {"start": v(35.06, 44.5) * mm, "end": v(35.06, 48.5) * mm});
            skLineSegment(sketch, "E56.bottom", {"start": v(50.44, 44.5) * mm, "end": v(61, 44.5) * mm});
            skLineSegment(sketch, "E56.top", {"start": v(50.44, 48.5) * mm, "end": v(61, 48.5) * mm});
            skLineSegment(sketch, "E56.left", {"start": v(50.44, 44.5) * mm, "end": v(50.44, 48.5) * mm});
            skLineSegment(sketch, "E56.right", {"start": v(61, 44.5) * mm, "end": v(61, 48.5) * mm});
            skLineSegment(sketch, "E57.bottom", {"start": v(76, 44.5) * mm, "end": v(83.5, 44.5) * mm});
            skLineSegment(sketch, "E57.top", {"start": v(76, 48.5) * mm, "end": v(83.5, 48.5) * mm});
            skLineSegment(sketch, "E57.left", {"start": v(76, 44.5) * mm, "end": v(76, 48.5) * mm});
            skLineSegment(sketch, "E57.right", {"start": v(83.5, 44.5) * mm, "end": v(83.5, 48.5) * mm});
            skLineSegment(sketch, "E58", {"start": v(-76, 48.5) * mm, "end": v(76, 48.5) * mm});
            skLineSegment(sketch, "E59", {"start": v(76, 44.5) * mm, "end": v(-76, 44.5) * mm});
            skSolve(sketch);
        }
        {
            var Q0;
            Q0=makeQuery(id+"F12.imprint","IMPRINT",FACE,{"disambiguationData":[TD([[makeQuery(id+"F12.imprint","IMPRINT",EDGE,{"derivedFrom":sQuery(id+"F12.wireOp",EDGE,"E51.bottom")}),1.0]])]});
            var Q1;
            {var subQ0=sQuery(id+"F12.wireOp",EDGE,"E51.right");Q1=makeQuery(id+"F12.imprint","IMPRINT",FACE,{"disambiguationData":[TD([[makeQuery(id+"F12.imprint","IMPRINT",EDGE,{"derivedFrom":subQ0}),-1.0]])]});}
            var Q2;
            {var subQ0=sQuery(id+"F12.wireOp",EDGE,"E52.left");Q2=makeQuery(id+"F12.imprint","IMPRINT",FACE,{"disambiguationData":[TD([[makeQuery(id+"F12.imprint","IMPRINT",EDGE,{"derivedFrom":subQ0}),-1.0]])]});}
            var Q3;
            {var subQ0=sQuery(id+"F12.wireOp",EDGE,"E52.right");Q3=makeQuery(id+"F12.imprint","IMPRINT",FACE,{"disambiguationData":[TD([[makeQuery(id+"F12.imprint","IMPRINT",EDGE,{"derivedFrom":subQ0}),-1.0]])]});}
            var Q4;
            {var subQ0=sQuery(id+"F12.wireOp",EDGE,"E53.left");Q4=makeQuery(id+"F12.imprint","IMPRINT",FACE,{"disambiguationData":[TD([[makeQuery(id+"F12.imprint","IMPRINT",EDGE,{"derivedFrom":subQ0}),-1.0]])]});}
            var Q5;
            {var subQ0=sQuery(id+"F12.wireOp",EDGE,"E53.right");Q5=makeQuery(id+"F12.imprint","IMPRINT",FACE,{"disambiguationData":[TD([[makeQuery(id+"F12.imprint","IMPRINT",EDGE,{"derivedFrom":subQ0}),-1.0]])]});}
            var Q6;
            {var subQ0=sQuery(id+"F12.wireOp",EDGE,"E54.left");Q6=makeQuery(id+"F12.imprint","IMPRINT",FACE,{"disambiguationData":[TD([[makeQuery(id+"F12.imprint","IMPRINT",EDGE,{"derivedFrom":subQ0}),-1.0]])]});}
            var Q7;
            {var subQ0=sQuery(id+"F12.wireOp",EDGE,"E54.right");Q7=makeQuery(id+"F12.imprint","IMPRINT",FACE,{"disambiguationData":[TD([[makeQuery(id+"F12.imprint","IMPRINT",EDGE,{"derivedFrom":subQ0}),-1.0]])]});}
            var Q8;
            {var subQ0=sQuery(id+"F12.wireOp",EDGE,"E55.left");Q8=makeQuery(id+"F12.imprint","IMPRINT",FACE,{"disambiguationData":[TD([[makeQuery(id+"F12.imprint","IMPRINT",EDGE,{"derivedFrom":subQ0}),-1.0]])]});}
            var Q9;
            {var subQ0=sQuery(id+"F12.wireOp",EDGE,"E55.right");Q9=makeQuery(id+"F12.imprint","IMPRINT",FACE,{"disambiguationData":[TD([[makeQuery(id+"F12.imprint","IMPRINT",EDGE,{"derivedFrom":subQ0}),-1.0]])]});}
            var Q10;
            {var subQ0=sQuery(id+"F12.wireOp",EDGE,"E56.left");Q10=makeQuery(id+"F12.imprint","IMPRINT",FACE,{"disambiguationData":[TD([[makeQuery(id+"F12.imprint","IMPRINT",EDGE,{"derivedFrom":subQ0}),-1.0]])]});}
            var Q11;
            {var subQ0=sQuery(id+"F12.wireOp",EDGE,"E56.right");Q11=makeQuery(id+"F12.imprint","IMPRINT",FACE,{"disambiguationData":[TD([[makeQuery(id+"F12.imprint","IMPRINT",EDGE,{"derivedFrom":subQ0}),-1.0]])]});}
            var Q12;
            Q12=makeQuery(id+"F12.imprint","IMPRINT",FACE,{"disambiguationData":[TD([[makeQuery(id+"F12.imprint","IMPRINT",EDGE,{"derivedFrom":sQuery(id+"F12.wireOp",EDGE,"E57.bottom")}),1.0]])]});
            extrude(context, id + "F13", {"entities" : qUnion([Q0, Q1, Q2, Q3, Q4, Q5, Q6, Q7, Q8, Q9, Q10, Q11, Q12]), "oppositeDirection" : true, "depth" : .4 * mm, "offsetDistance" : 25 * mm});
        }
        {
            var Q0;
            Q0=makeQuery(id+"F12.imprint","IMPRINT",FACE,{"disambiguationData":[TD([[makeQuery(id+"F12.imprint","IMPRINT",EDGE,{"derivedFrom":sQuery(id+"F12.wireOp",EDGE,"E51.bottom")}),1.0]])]});
            var Q1;
            Q1=makeQuery(id+"F12.imprint","IMPRINT",FACE,{"disambiguationData":[TD([[makeQuery(id+"F12.imprint","IMPRINT",EDGE,{"derivedFrom":sQuery(id+"F12.wireOp",EDGE,"E57.bottom")}),1.0]])]});
            var Q2;
            {var subQ0=sQuery(id+"F12.wireOp",EDGE,"E52.left");Q2=makeQuery(id+"F12.imprint","IMPRINT",FACE,{"disambiguationData":[TD([[makeQuery(id+"F12.imprint","IMPRINT",EDGE,{"derivedFrom":subQ0}),-1.0]])]});}
            var Q3;
            {var subQ0=sQuery(id+"F12.wireOp",EDGE,"E53.left");Q3=makeQuery(id+"F12.imprint","IMPRINT",FACE,{"disambiguationData":[TD([[makeQuery(id+"F12.imprint","IMPRINT",EDGE,{"derivedFrom":subQ0}),-1.0]])]});}
            var Q4;
            {var subQ0=sQuery(id+"F12.wireOp",EDGE,"E54.left");Q4=makeQuery(id+"F12.imprint","IMPRINT",FACE,{"disambiguationData":[TD([[makeQuery(id+"F12.imprint","IMPRINT",EDGE,{"derivedFrom":subQ0}),-1.0]])]});}
            var Q5;
            {var subQ0=sQuery(id+"F12.wireOp",EDGE,"E55.left");Q5=makeQuery(id+"F12.imprint","IMPRINT",FACE,{"disambiguationData":[TD([[makeQuery(id+"F12.imprint","IMPRINT",EDGE,{"derivedFrom":subQ0}),-1.0]])]});}
            var Q6;
            {var subQ0=sQuery(id+"F12.wireOp",EDGE,"E56.left");Q6=makeQuery(id+"F12.imprint","IMPRINT",FACE,{"disambiguationData":[TD([[makeQuery(id+"F12.imprint","IMPRINT",EDGE,{"derivedFrom":subQ0}),-1.0]])]});}
            var Q7;
            {var subQ0=sQuery(id+"F5.wireOp",EDGE,"E28.top");var subQ1=makeQuery(id+"F5.imprint","INTERSECT",VERTEX,{"derivedFrom":[subQ0,sQuery(id+"F5.wireOp",EDGE,"E46")]});var subQ2=sQuery(id+"F5.wireOp",EDGE,"E31");var subQ4=makeQuery(id+"F5.imprint","INTERSECT",VERTEX,{"disambiguationData":[OD(0.0)],"derivedFrom":[subQ0,subQ2]});var subQ5=makeQuery(id+"F5.imprint","INTERSECT",VERTEX,{"derivedFrom":[subQ0,sQuery(id+"F5.wireOp",EDGE,"E45")]});Q7=makeQuery(id+"F10.opChamfer","SPLIT",FACE,{"disambiguationData":[OD(0.0)],"derivedFrom":makeQuery(id+"F9.boolean.opBoolean","MERGE",FACE,{"derivedFrom":[makeQuery(id+"F8.opExtrude","SWEPT_FACE",FACE,{"disambiguationData":[OSD([subQ0]),TDD([makeQuery(id+"F5.imprint","IMPRINT",EDGE,{"disambiguationData":[TD([[subQ5,1.0]])],"derivedFrom":subQ0})])]}),makeQuery(id+"F8.opExtrude","SWEPT_FACE",FACE,{"disambiguationData":[OSD([subQ0]),TDD([makeQuery(id+"F5.imprint","IMPRINT",EDGE,{"disambiguationData":[TD([[subQ1,-1.0]])],"derivedFrom":subQ0})])]}),makeQuery(id+"F9.opExtrude","SWEPT_FACE",FACE,{"disambiguationData":[OSD([subQ0]),TDD([makeQuery(id+"F5.imprint","IMPRINT",EDGE,{"disambiguationData":[TD([[subQ5,-1.0]])],"derivedFrom":subQ0}),makeQuery(id+"F5.imprint","IMPRINT",EDGE,{"disambiguationData":[TD([[subQ4,-1.0]])],"derivedFrom":subQ0}),makeQuery(id+"F5.imprint","IMPRINT",EDGE,{"disambiguationData":[TD([[subQ1,1.0]])],"derivedFrom":subQ0})])]})]})});}
            extrude(context, id + "F14", {"entities" : qUnion([Q0, Q1, Q2, Q3, Q4, Q5, Q6]), "operationType" : NewBodyOperationType.ADD, "endBound" : BoundingType.UP_TO_SURFACE, "oppositeDirection" : true, "depth" : 25 * mm, "endBoundEntityFace" : qUnion([Q7]), "hasOffset" : true, "offsetDistance" : 0.2 * mm});
        }
    });
